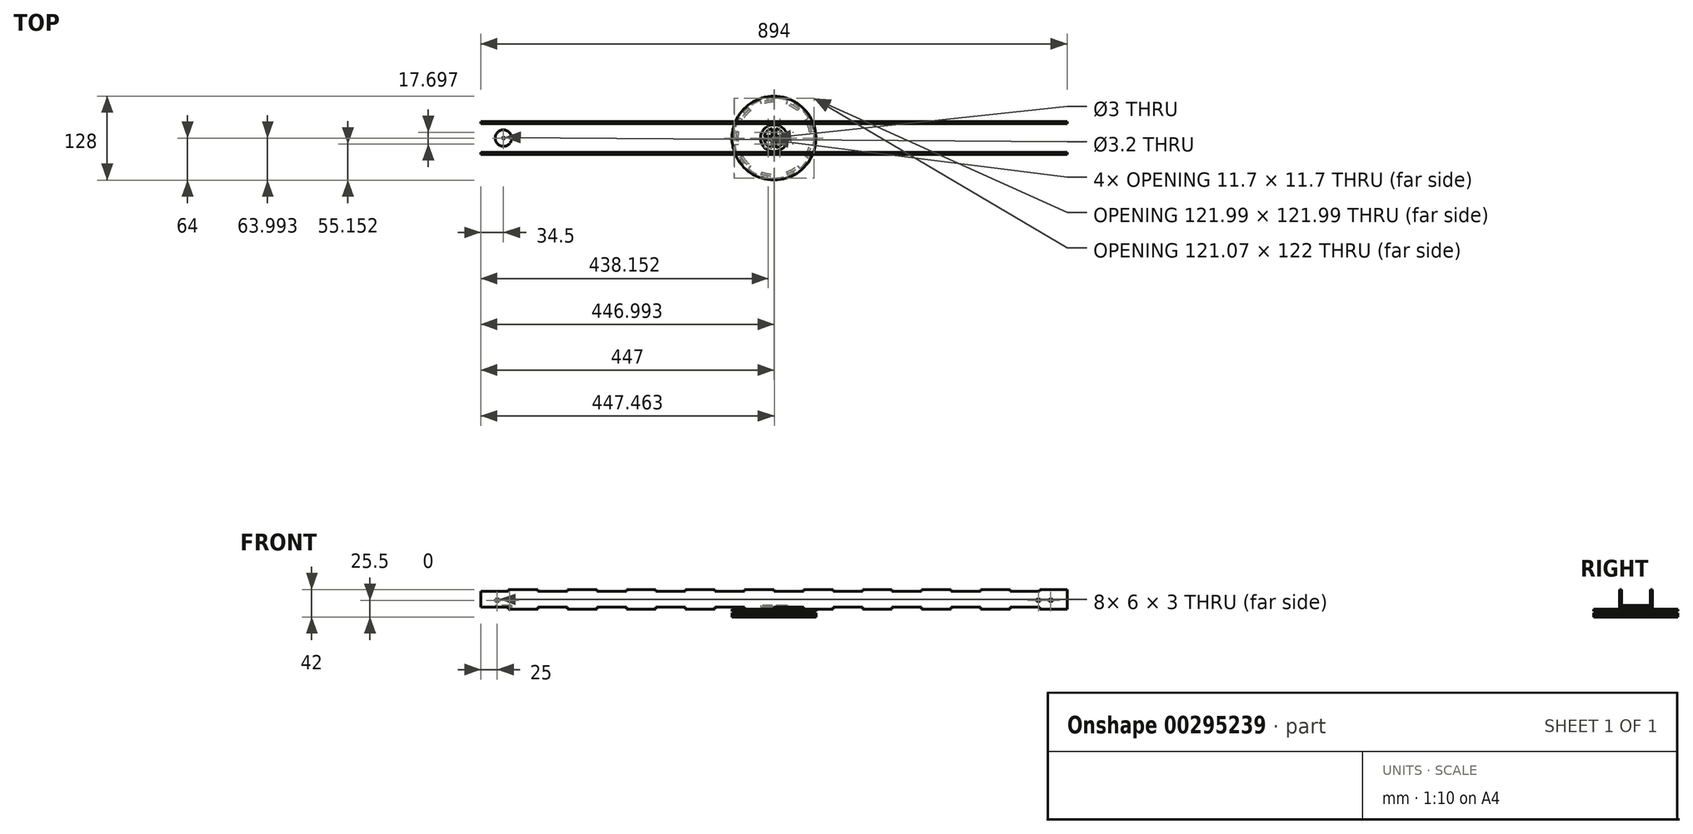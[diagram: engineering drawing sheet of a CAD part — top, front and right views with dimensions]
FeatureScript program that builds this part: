
annotation { "Feature Type Name" : "Feature", "Feature Type Description" : "" }
export const myFeature = defineFeature(function(context is Context, id is Id, definition is map)
    precondition{}
    {
        {
            assignVariable(context, id + "F0", {"name" : "WT", "anyValue" : 3});
        }
        {
            var Q0;
            Q0=qCreatedBy(makeId("Top.planeOp"),FACE);
            var sketch = newSketch(context, id + "F1", { "sketchPlane" : qUnion([Q0])});
            skCircle(sketch, "E0", {"center": v(0, 0) * mm, "radius": 60 * mm});
            skLineSegment(sketch, "E1.bottom", {"start": v(-450, 25) * mm, "end": v(450, 25) * mm});
            skLineSegment(sketch, "E1.top", {"start": v(-450, -25) * mm, "end": v(450, -25) * mm});
            skLineSegment(sketch, "E1.left", {"start": v(-450, 25) * mm, "end": v(-450, -25) * mm});
            skLineSegment(sketch, "E1.right", {"start": v(450, 25) * mm, "end": v(450, -25) * mm});
            skLineSegment(sketch, "E2", {"start": v(-450, 0) * mm, "end": v(450, 0) * mm, "construction": true});
            skCircle(sketch, "E3", {"center": v(-412.5, 0) * mm, "radius": 12.5 * mm});
            skCircle(sketch, "E4", {"center": v(0, 0) * mm, "radius": 64 * mm});
            skCircle(sketch, "E5", {"center": v(0, 0) * mm, "radius": 30 * mm});
            skCircle(sketch, "E6", {"center": v(0, 0) * mm, "radius": 27 * mm});
            skLineSegment(sketch, "E7", {"start": v(-30, 0) * mm, "end": v(0, 0) * mm});
            skLineSegment(sketch, "E8", {"start": v(0, 30) * mm, "end": v(0, 0) * mm});
            skLineSegment(sketch, "E9", {"start": v(0, 0) * mm, "end": v(30, 0) * mm});
            skLineSegment(sketch, "E10", {"start": v(0, 0) * mm, "end": v(0, -30) * mm});
            skPoint(sketch, "E10.endSnap0", {"position": v(0, -25) * mm});
            skLineSegment(sketch, "E11.bottom", {"start": v(-375, 10) * mm, "end": v(375, 10) * mm});
            skLineSegment(sketch, "E11.top", {"start": v(-375, -10) * mm, "end": v(375, -10) * mm});
            skLineSegment(sketch, "E11.left", {"start": v(-375, 10) * mm, "end": v(-375, -10) * mm});
            skLineSegment(sketch, "E11.right", {"start": v(375, 10) * mm, "end": v(375, -10) * mm});
            skLineSegment(sketch, "E12.bottom", {"start": v(-447, 22) * mm, "end": v(447, 22) * mm});
            skLineSegment(sketch, "E12.top", {"start": v(-447, -22) * mm, "end": v(447, -22) * mm});
            skLineSegment(sketch, "E12.left", {"start": v(-447, 22) * mm, "end": v(-447, -22) * mm});
            skLineSegment(sketch, "E12.right", {"start": v(447, 22) * mm, "end": v(447, -22) * mm});
            skCircle(sketch, "E13.MirrorC", {"center": v(412.5, 0) * mm, "radius": 12.5 * mm});
            skSolve(sketch);
        }
        {
            var Q0;
            Q0=qCreatedBy(makeId("Top.planeOp"),FACE);
            cPlane(context, id + "F2", {"entities" : qUnion([Q0]), "cplaneType" : CPlaneType.OFFSET, "offset" : (getVariable(context, 'WT')) * mm, "width" : 150 * mm, "height" : 150 * mm});
        }
        {
            var Q0;
            Q0=qCreatedBy(makeId("Top.planeOp"),FACE);
            var sketch = newSketch(context, id + "F3", { "sketchPlane" : qUnion([Q0])});
            skCircle(sketch, "E14.0", {"center": v(0, 0) * mm, "radius": 64 * mm});
            skLineSegment(sketch, "E15.0", {"start": v(-450, 25) * mm, "end": v(450, 25) * mm, "construction": true});
            skLineSegment(sketch, "E16.0", {"start": v(-450, -25) * mm, "end": v(450, -25) * mm, "construction": true});
            skCircle(sketch, "E17", {"center": v(0, 0) * mm, "radius": 15 * mm});
            skLineSegment(sketch, "E18.0", {"start": v(-447, 22) * mm, "end": v(447, 22) * mm, "construction": true});
            skLineSegment(sketch, "E18.1", {"start": v(-447, -22) * mm, "end": v(447, -22) * mm, "construction": true});
            skLineSegment(sketch, "E19.0", {"start": v(-375, -10) * mm, "end": v(375, -10) * mm, "construction": true});
            skLineSegment(sketch, "E19.1", {"start": v(-375, 10) * mm, "end": v(375, 10) * mm, "construction": true});
            skLineSegment(sketch, "E20", {"start": v(-15, 0) * mm, "end": v(15, 0) * mm, "construction": true});
            skLineSegment(sketch, "E21", {"start": v(-14.7, 3) * mm, "end": v(14.7, 3) * mm});
            skLineSegment(sketch, "E22.MirrorCS", {"start": v(-14.7, -3) * mm, "end": v(14.7, -3) * mm});
            skLineSegment(sketch, "E23", {"start": v(-3, 3) * mm, "end": v(-3, 14.7) * mm});
            skLineSegment(sketch, "E24.MirrorCS", {"start": v(3, 3) * mm, "end": v(3, 14.7) * mm});
            skLineSegment(sketch, "E25.MirrorCS", {"start": v(-3, -3) * mm, "end": v(-3, -14.7) * mm});
            skLineSegment(sketch, "E26.MirrorCS", {"start": v(3, -3) * mm, "end": v(3, -14.7) * mm});
            skCircle(sketch, "E27", {"center": v(0, 0) * mm, "radius": 20.5 * mm});
            skCircle(sketch, "E28", {"center": v(0, 0) * mm, "radius": 1.5 * mm});
            skLineSegment(sketch, "E29", {"start": v(-3, 3) * mm, "end": v(-3, -3) * mm});
            skLineSegment(sketch, "E30", {"start": v(3, -3) * mm, "end": v(3, 3) * mm});
            skLineSegment(sketch, "E31", {"start": v(-3, -9.5) * mm, "end": v(3, -9.5) * mm});
            skLineSegment(sketch, "E32.MirrorCS", {"start": v(-3, 9.5) * mm, "end": v(3, 9.5) * mm});
            skSolve(sketch);
        }
        {
            var Q0;
            Q0=qCreatedBy(makeId("Top.planeOp"),FACE);
            cPlane(context, id + "F4", {"entities" : qUnion([Q0]), "cplaneType" : CPlaneType.OFFSET, "offset" : (getVariable(context, 'WT')) * mm, "width" : 150 * mm, "height" : 150 * mm});
        }
        {
            var Q0;
            Q0=qCreatedBy(id+"F4.planeOp",FACE);
            var sketch = newSketch(context, id + "F5", { "sketchPlane" : qUnion([Q0])});
            skCircle(sketch, "E33.0", {"center": v(0, 0) * mm, "radius": 20.5 * mm});
            skCircle(sketch, "E34.0", {"center": v(0, 0) * mm, "radius": 15 * mm});
            skLineSegment(sketch, "E35.0", {"start": v(3, -3) * mm, "end": v(3, -14.7) * mm});
            skLineSegment(sketch, "E35.1", {"start": v(-3, -3) * mm, "end": v(-3, -14.7) * mm});
            skLineSegment(sketch, "E35.2", {"start": v(-14.7, -3) * mm, "end": v(14.7, -3) * mm});
            skLineSegment(sketch, "E35.3", {"start": v(-14.7, 3) * mm, "end": v(14.7, 3) * mm});
            skLineSegment(sketch, "E35.4", {"start": v(-3, 3) * mm, "end": v(-3, 14.7) * mm});
            skLineSegment(sketch, "E35.5", {"start": v(3, 3) * mm, "end": v(3, 14.7) * mm});
            skSolve(sketch);
        }
        {
            var Q0;
            Q0=qCreatedBy(id+"F2.planeOp",FACE);
            var sketch = newSketch(context, id + "F6", { "sketchPlane" : qUnion([Q0])});
            skLineSegment(sketch, "E36.0", {"start": v(-450, 25) * mm, "end": v(450, 25) * mm});
            skLineSegment(sketch, "E36.1", {"start": v(-447, 22) * mm, "end": v(447, 22) * mm});
            skLineSegment(sketch, "E36.2", {"start": v(-375, 10) * mm, "end": v(375, 10) * mm});
            skLineSegment(sketch, "E36.3", {"start": v(-375, -10) * mm, "end": v(375, -10) * mm});
            skLineSegment(sketch, "E36.4", {"start": v(-447, -22) * mm, "end": v(447, -22) * mm});
            skLineSegment(sketch, "E36.5", {"start": v(-450, -25) * mm, "end": v(450, -25) * mm});
            skLineSegment(sketch, "E36.6", {"start": v(375, 10) * mm, "end": v(375, -10) * mm});
            skLineSegment(sketch, "E36.7", {"start": v(447, 22) * mm, "end": v(447, -22) * mm});
            skLineSegment(sketch, "E36.8", {"start": v(450, 25) * mm, "end": v(450, -25) * mm});
            skLineSegment(sketch, "E36.9", {"start": v(-375, 10) * mm, "end": v(-375, -10) * mm});
            skLineSegment(sketch, "E36.10", {"start": v(-447, 22) * mm, "end": v(-447, -22) * mm});
            skLineSegment(sketch, "E36.11", {"start": v(-450, 25) * mm, "end": v(-450, -25) * mm});
            skCircle(sketch, "E37.0", {"center": v(-412.5, 0) * mm, "radius": 12.5 * mm});
            skCircle(sketch, "E38", {"center": v(-412.5, 0) * mm, "radius": 1.6 * mm});
            skLineSegment(sketch, "E39", {"start": v(-450, 8.33) * mm, "end": v(-447, 8.33) * mm});
            skLineSegment(sketch, "E40", {"start": v(-450, -8.33) * mm, "end": v(-447, -8.33) * mm});
            skPoint(sketch, "E40.endSnap0", {"position": v(-447, 0) * mm});
            skLineSegment(sketch, "E41", {"start": v(0, 22) * mm, "end": v(0, 25) * mm});
            skLineSegment(sketch, "E42", {"start": v(-447, 22) * mm, "end": v(-450, 22) * mm});
            skLineSegment(sketch, "E43", {"start": v(-447, -22) * mm, "end": v(-450, -22) * mm});
            skLineSegment(sketch, "E44", {"start": v(-405, 22) * mm, "end": v(-405, 25) * mm});
            skLineSegment(sketch, "E45.0.1.0", {"start": v(-405, -25) * mm, "end": v(-405, -22) * mm});
            skLineSegment(sketch, "E45.1.0.0", {"start": v(-360, 22) * mm, "end": v(-360, 25) * mm});
            skLineSegment(sketch, "E45.1.1.0", {"start": v(-360, -25) * mm, "end": v(-360, -22) * mm});
            skLineSegment(sketch, "E45.2.0.0", {"start": v(-315, 22) * mm, "end": v(-315, 25) * mm});
            skLineSegment(sketch, "E45.2.1.0", {"start": v(-315, -25) * mm, "end": v(-315, -22) * mm});
            skLineSegment(sketch, "E45.3.0.0", {"start": v(-270, 22) * mm, "end": v(-270, 25) * mm});
            skLineSegment(sketch, "E45.3.1.0", {"start": v(-270, -25) * mm, "end": v(-270, -22) * mm});
            skLineSegment(sketch, "E45.4.0.0", {"start": v(-225, 22) * mm, "end": v(-225, 25) * mm});
            skLineSegment(sketch, "E45.4.1.0", {"start": v(-225, -25) * mm, "end": v(-225, -22) * mm});
            skLineSegment(sketch, "E45.5.0.0", {"start": v(-180, 22) * mm, "end": v(-180, 25) * mm});
            skLineSegment(sketch, "E45.5.1.0", {"start": v(-180, -25) * mm, "end": v(-180, -22) * mm});
            skLineSegment(sketch, "E45.6.0.0", {"start": v(-135, 22) * mm, "end": v(-135, 25) * mm});
            skLineSegment(sketch, "E45.6.1.0", {"start": v(-135, -25) * mm, "end": v(-135, -22) * mm});
            skLineSegment(sketch, "E45.7.0.0", {"start": v(-90, 22) * mm, "end": v(-90, 25) * mm});
            skLineSegment(sketch, "E45.7.1.0", {"start": v(-90, -25) * mm, "end": v(-90, -22) * mm});
            skLineSegment(sketch, "E45.8.0.0", {"start": v(-45, 22) * mm, "end": v(-45, 25) * mm});
            skLineSegment(sketch, "E45.8.1.0", {"start": v(-45, -25) * mm, "end": v(-45, -22) * mm});
            skLineSegment(sketch, "E45.9.1.0", {"start": v(0, -25) * mm, "end": v(0, -22) * mm});
            skLineSegment(sketch, "E45.10.0.0", {"start": v(45, 22) * mm, "end": v(45, 25) * mm});
            skLineSegment(sketch, "E45.10.1.0", {"start": v(45, -25) * mm, "end": v(45, -22) * mm});
            skLineSegment(sketch, "E45.11.0.0", {"start": v(90, 22) * mm, "end": v(90, 25) * mm});
            skLineSegment(sketch, "E45.11.1.0", {"start": v(90, -25) * mm, "end": v(90, -22) * mm});
            skLineSegment(sketch, "E45.12.0.0", {"start": v(135, 22) * mm, "end": v(135, 25) * mm});
            skLineSegment(sketch, "E45.12.1.0", {"start": v(135, -25) * mm, "end": v(135, -22) * mm});
            skLineSegment(sketch, "E45.13.0.0", {"start": v(180, 22) * mm, "end": v(180, 25) * mm});
            skLineSegment(sketch, "E45.13.1.0", {"start": v(180, -25) * mm, "end": v(180, -22) * mm});
            skLineSegment(sketch, "E45.14.0.0", {"start": v(225, 22) * mm, "end": v(225, 25) * mm});
            skLineSegment(sketch, "E45.14.1.0", {"start": v(225, -25) * mm, "end": v(225, -22) * mm});
            skLineSegment(sketch, "E45.15.0.0", {"start": v(270, 22) * mm, "end": v(270, 25) * mm});
            skLineSegment(sketch, "E45.15.1.0", {"start": v(270, -25) * mm, "end": v(270, -22) * mm});
            skLineSegment(sketch, "E45.16.0.0", {"start": v(315, 22) * mm, "end": v(315, 25) * mm});
            skLineSegment(sketch, "E45.16.1.0", {"start": v(315, -25) * mm, "end": v(315, -22) * mm});
            skLineSegment(sketch, "E45.17.0.0", {"start": v(360, 22) * mm, "end": v(360, 25) * mm});
            skLineSegment(sketch, "E45.17.1.0", {"start": v(360, -25) * mm, "end": v(360, -22) * mm});
            skLineSegment(sketch, "E45.18.0.0", {"start": v(405, 22) * mm, "end": v(405, 25) * mm});
            skLineSegment(sketch, "E45.18.1.0", {"start": v(405, -25) * mm, "end": v(405, -22) * mm});
            skLineSegment(sketch, "E45.direction1", {"start": v(-405, 22) * mm, "end": v(-360, 22) * mm, "construction": true});
            skLineSegment(sketch, "E45.direction2", {"start": v(-405, 22) * mm, "end": v(-405, -25) * mm, "construction": true});
            skLineSegment(sketch, "E46.MirrorCS", {"start": v(447, 22) * mm, "end": v(450, 22) * mm});
            skLineSegment(sketch, "E47.MirrorCS", {"start": v(450, 8.33) * mm, "end": v(447, 8.33) * mm});
            skLineSegment(sketch, "E48.MirrorCS", {"start": v(450, -8.33) * mm, "end": v(447, -8.33) * mm});
            skLineSegment(sketch, "E49.MirrorCS", {"start": v(447, -22) * mm, "end": v(450, -22) * mm});
            skCircle(sketch, "E50", {"center": v(-435.5, 0) * mm, "radius": 2.5 * mm});
            skCircle(sketch, "E51", {"center": v(-386.6, -10.4) * mm, "radius": 1.6 * mm});
            skLineSegment(sketch, "E52", {"start": v(-400, 0) * mm, "end": v(-375, 0) * mm, "construction": true});
            skPoint(sketch, "E52.startSnap0", {"position": v(-450, 0) * mm});
            skCircle(sketch, "E53.MirrorC", {"center": v(-386.6, 10.4) * mm, "radius": 1.6 * mm});
            skCircle(sketch, "E54.MirrorC", {"center": v(386.6, 10.4) * mm, "radius": 1.6 * mm});
            skCircle(sketch, "E55.MirrorC", {"center": v(386.6, -10.4) * mm, "radius": 1.6 * mm});
            skCircle(sketch, "E56.MirrorC", {"center": v(412.5, 0) * mm, "radius": 1.6 * mm});
            skCircle(sketch, "E57.MirrorC", {"center": v(412.5, 0) * mm, "radius": 12.5 * mm});
            skCircle(sketch, "E58.MirrorC", {"center": v(435.5, 0) * mm, "radius": 2.5 * mm});
            skSolve(sketch);
        }
        {
            var Q0;
            Q0=sQuery(id+"F1.wireOp",EDGE,"E1.top");
            cPlane(context, id + "F7", {"entities" : qUnion([Q0]), "cplaneType" : CPlaneType.LINE_ANGLE, "offset" : 25 * mm, "angle" : 0 * degree, "width" : 150 * mm, "height" : 150 * mm});
        }
        {
            var Q0;
            Q0=qCreatedBy(id+"F7.planeOp",FACE);
            var sketch = newSketch(context, id + "F8", { "sketchPlane" : qUnion([Q0])});
            skLineSegment(sketch, "E59.0", {"start": v(450, 0) * mm, "end": v(-450, 0) * mm});
            skLineSegment(sketch, "E60", {"start": v(450, 0) * mm, "end": v(450, 30) * mm});
            skLineSegment(sketch, "E61", {"start": v(450, 30) * mm, "end": v(-450, 30) * mm});
            skLineSegment(sketch, "E62", {"start": v(-450, 30) * mm, "end": v(-450, 0) * mm});
            skSolve(sketch);
        }
        {
            var Q0;
            Q0=sQuery(id+"F1.wireOp",EDGE,"E1.bottom");
            cPlane(context, id + "F9", {"entities" : qUnion([Q0]), "cplaneType" : CPlaneType.LINE_ANGLE, "offset" : 25 * mm, "angle" : 0 * degree, "width" : 150 * mm, "height" : 150 * mm});
        }
        {
            var Q0;
            Q0=qCreatedBy(id+"F9.planeOp",FACE);
            var sketch = newSketch(context, id + "F10", { "sketchPlane" : qUnion([Q0])});
            skLineSegment(sketch, "E63.0", {"start": v(450, 0) * mm, "end": v(-450, 0) * mm});
            skLineSegment(sketch, "E64.0", {"start": v(-450, 30) * mm, "end": v(-450, 0) * mm});
            skLineSegment(sketch, "E64.1", {"start": v(450, 30) * mm, "end": v(-450, 30) * mm});
            skLineSegment(sketch, "E64.2", {"start": v(450, 0) * mm, "end": v(450, 30) * mm});
            skSolve(sketch);
        }
        {
            var Q0;
            Q0=sQuery(id+"F1.wireOp",EDGE,"E1.right");
            cPlane(context, id + "F11", {"entities" : qUnion([Q0]), "cplaneType" : CPlaneType.LINE_ANGLE, "offset" : 25 * mm, "angle" : 90 * degree, "width" : 150 * mm, "height" : 150 * mm});
        }
        {
            var Q0;
            Q0=qCreatedBy(id+"F11.planeOp",FACE);
            var sketch = newSketch(context, id + "F12", { "sketchPlane" : qUnion([Q0])});
            skLineSegment(sketch, "E65.0", {"start": v(25, 0) * mm, "end": v(-25, 0) * mm});
            skLineSegment(sketch, "E66.0", {"start": v(-25, 30) * mm, "end": v(-25, 0) * mm});
            skLineSegment(sketch, "E67", {"start": v(-25, 30) * mm, "end": v(25, 30) * mm});
            skLineSegment(sketch, "E68", {"start": v(25, 30) * mm, "end": v(25, 0) * mm});
            skSolve(sketch);
        }
        {
            var Q0;
            Q0=sQuery(id+"F1.wireOp",EDGE,"E1.left");
            cPlane(context, id + "F13", {"entities" : qUnion([Q0]), "cplaneType" : CPlaneType.LINE_ANGLE, "offset" : 25 * mm, "angle" : 90 * degree, "width" : 150 * mm, "height" : 150 * mm});
        }
        {
            var Q0;
            Q0=qCreatedBy(id+"F13.planeOp",FACE);
            var sketch = newSketch(context, id + "F14", { "sketchPlane" : qUnion([Q0])});
            skLineSegment(sketch, "E69.0", {"start": v(25, 0) * mm, "end": v(-25, 0) * mm});
            skLineSegment(sketch, "E70.0", {"start": v(25, 30) * mm, "end": v(25, 0) * mm});
            skLineSegment(sketch, "E71.0", {"start": v(-25, 30) * mm, "end": v(25, 30) * mm});
            skLineSegment(sketch, "E72.0", {"start": v(-25, 30) * mm, "end": v(-25, 0) * mm});
            skSolve(sketch);
        }
        {
            var Q0;
            Q0=sQuery(id+"F8.wireOp",EDGE,"E61");
            cPlane(context, id + "F15", {"entities" : qUnion([Q0]), "cplaneType" : CPlaneType.LINE_ANGLE, "offset" : 25 * mm, "angle" : 90 * degree, "width" : 150 * mm, "height" : 150 * mm});
        }
        {
            var Q0;
            Q0=qCreatedBy(id+"F15.planeOp",FACE);
            var sketch = newSketch(context, id + "F16", { "sketchPlane" : qUnion([Q0])});
            skLineSegment(sketch, "E73.0", {"start": v(-450, 25) * mm, "end": v(450, 25) * mm});
            skLineSegment(sketch, "E73.1", {"start": v(-450, -25) * mm, "end": v(450, -25) * mm});
            skLineSegment(sketch, "E73.2", {"start": v(450, 25) * mm, "end": v(450, -25) * mm});
            skLineSegment(sketch, "E73.3", {"start": v(-450, 25) * mm, "end": v(-450, -25) * mm});
            skLineSegment(sketch, "E74.0", {"start": v(-447, 22) * mm, "end": v(-447, -22) * mm});
            skLineSegment(sketch, "E75.0", {"start": v(-447, 22) * mm, "end": v(-450, 22) * mm});
            skLineSegment(sketch, "E75.1", {"start": v(-450, 8.33) * mm, "end": v(-447, 8.33) * mm});
            skLineSegment(sketch, "E75.2", {"start": v(-450, -8.33) * mm, "end": v(-447, -8.33) * mm});
            skLineSegment(sketch, "E75.3", {"start": v(-447, -22) * mm, "end": v(-450, -22) * mm});
            skLineSegment(sketch, "E76.0", {"start": v(-447, -22) * mm, "end": v(447, -22) * mm});
            skLineSegment(sketch, "E77.0", {"start": v(-447, 22) * mm, "end": v(447, 22) * mm});
            skLineSegment(sketch, "E78.0", {"start": v(-405, 22) * mm, "end": v(-405, 25) * mm});
            skLineSegment(sketch, "E78.1", {"start": v(-405, -25) * mm, "end": v(-405, -22) * mm});
            skLineSegment(sketch, "E78.2", {"start": v(-360, 22) * mm, "end": v(-360, 25) * mm});
            skLineSegment(sketch, "E78.3", {"start": v(-360, -25) * mm, "end": v(-360, -22) * mm});
            skLineSegment(sketch, "E78.4", {"start": v(-315, -25) * mm, "end": v(-315, -22) * mm});
            skLineSegment(sketch, "E78.5", {"start": v(-315, 22) * mm, "end": v(-315, 25) * mm});
            skLineSegment(sketch, "E78.6", {"start": v(-270, 22) * mm, "end": v(-270, 25) * mm});
            skLineSegment(sketch, "E78.7", {"start": v(-270, -25) * mm, "end": v(-270, -22) * mm});
            skLineSegment(sketch, "E78.8", {"start": v(-225, -25) * mm, "end": v(-225, -22) * mm});
            skLineSegment(sketch, "E78.9", {"start": v(-225, 22) * mm, "end": v(-225, 25) * mm});
            skLineSegment(sketch, "E78.10", {"start": v(-180, 22) * mm, "end": v(-180, 25) * mm});
            skLineSegment(sketch, "E78.11", {"start": v(-180, -25) * mm, "end": v(-180, -22) * mm});
            skLineSegment(sketch, "E78.12", {"start": v(-135, 22) * mm, "end": v(-135, 25) * mm});
            skLineSegment(sketch, "E78.13", {"start": v(-135, -25) * mm, "end": v(-135, -22) * mm});
            skLineSegment(sketch, "E78.14", {"start": v(-90, 22) * mm, "end": v(-90, 25) * mm});
            skLineSegment(sketch, "E78.15", {"start": v(-90, -25) * mm, "end": v(-90, -22) * mm});
            skLineSegment(sketch, "E78.16", {"start": v(-45, 22) * mm, "end": v(-45, 25) * mm});
            skLineSegment(sketch, "E78.17", {"start": v(-45, -25) * mm, "end": v(-45, -22) * mm});
            skLineSegment(sketch, "E78.18", {"start": v(0, 22) * mm, "end": v(0, 25) * mm});
            skLineSegment(sketch, "E78.19", {"start": v(0, -25) * mm, "end": v(0, -22) * mm});
            skLineSegment(sketch, "E78.20", {"start": v(45, 22) * mm, "end": v(45, 25) * mm});
            skLineSegment(sketch, "E78.21", {"start": v(45, -25) * mm, "end": v(45, -22) * mm});
            skLineSegment(sketch, "E79.0", {"start": v(90, 22) * mm, "end": v(90, 25) * mm});
            skLineSegment(sketch, "E79.1", {"start": v(90, -25) * mm, "end": v(90, -22) * mm});
            skLineSegment(sketch, "E79.2", {"start": v(135, 22) * mm, "end": v(135, 25) * mm});
            skLineSegment(sketch, "E79.3", {"start": v(135, -25) * mm, "end": v(135, -22) * mm});
            skLineSegment(sketch, "E79.4", {"start": v(180, 22) * mm, "end": v(180, 25) * mm});
            skLineSegment(sketch, "E79.5", {"start": v(180, -25) * mm, "end": v(180, -22) * mm});
            skLineSegment(sketch, "E79.6", {"start": v(225, 22) * mm, "end": v(225, 25) * mm});
            skLineSegment(sketch, "E79.7", {"start": v(225, -25) * mm, "end": v(225, -22) * mm});
            skPoint(sketch, "E79.8", {"position": v(225, -23.5) * mm});
            skLineSegment(sketch, "E80.0", {"start": v(270, 22) * mm, "end": v(270, 25) * mm});
            skLineSegment(sketch, "E80.1", {"start": v(270, -25) * mm, "end": v(270, -22) * mm});
            skLineSegment(sketch, "E80.2", {"start": v(315, 22) * mm, "end": v(315, 25) * mm});
            skLineSegment(sketch, "E80.3", {"start": v(315, -25) * mm, "end": v(315, -22) * mm});
            skLineSegment(sketch, "E80.4", {"start": v(360, 22) * mm, "end": v(360, 25) * mm});
            skLineSegment(sketch, "E80.5", {"start": v(360, -25) * mm, "end": v(360, -22) * mm});
            skLineSegment(sketch, "E80.6", {"start": v(405, 22) * mm, "end": v(405, 25) * mm});
            skLineSegment(sketch, "E80.7", {"start": v(405, -25) * mm, "end": v(405, -22) * mm});
            skLineSegment(sketch, "E80.8", {"start": v(450, 8.33) * mm, "end": v(447, 8.33) * mm});
            skLineSegment(sketch, "E80.9", {"start": v(447, 22) * mm, "end": v(450, 22) * mm});
            skLineSegment(sketch, "E80.10", {"start": v(450, -8.33) * mm, "end": v(447, -8.33) * mm});
            skLineSegment(sketch, "E80.11", {"start": v(447, -22) * mm, "end": v(450, -22) * mm});
            skLineSegment(sketch, "E81.0", {"start": v(447, 22) * mm, "end": v(447, -22) * mm});
            skSolve(sketch);
        }
        {
            var Q0;
            Q0=qCreatedBy(id+"F2.planeOp",FACE);
            cPlane(context, id + "F17", {"entities" : qUnion([Q0]), "cplaneType" : CPlaneType.OFFSET, "offset" : (getVariable(context, 'WT')) * 3 * mm, "width" : 150 * mm, "height" : 150 * mm});
        }
        {
            var Q0;
            Q0=qCreatedBy(id+"F17.planeOp",FACE);
            var sketch = newSketch(context, id + "F18", { "sketchPlane" : qUnion([Q0])});
            skCircle(sketch, "E82.0", {"center": v(-412.5, 0) * mm, "radius": 1.6 * mm});
            skCircle(sketch, "E83.0", {"center": v(-412.5, 0) * mm, "radius": 12.5 * mm, "construction": true});
            skLineSegment(sketch, "E84.0", {"start": v(-450, 25) * mm, "end": v(450, 25) * mm});
            skLineSegment(sketch, "E85.0", {"start": v(-450, -25) * mm, "end": v(450, -25) * mm});
            skLineSegment(sketch, "E86", {"start": v(-425, -25) * mm, "end": v(-425, 25) * mm});
            skLineSegment(sketch, "E87", {"start": v(-400, 25) * mm, "end": v(-400, -25) * mm});
            skLineSegment(sketch, "E88.0", {"start": v(-447, -22) * mm, "end": v(-425, -22) * mm, "construction": true});
            skLineSegment(sketch, "E89", {"start": v(-419, 25) * mm, "end": v(-419, 22) * mm});
            skLineSegment(sketch, "E90", {"start": v(-412.5, 0) * mm, "end": v(-412.5, 12.5) * mm, "construction": true});
            skLineSegment(sketch, "E91.MirrorCS", {"start": v(-406, 25) * mm, "end": v(-406, 22) * mm});
            skLineSegment(sketch, "E92.MirrorCS", {"start": v(-406, -25) * mm, "end": v(-406, -22) * mm});
            skLineSegment(sketch, "E93.MirrorCS", {"start": v(-419, -25) * mm, "end": v(-419, -22) * mm});
            skLineSegment(sketch, "E94.0", {"start": v(-447, 22) * mm, "end": v(-425, 22) * mm});
            skPoint(sketch, "E95.start.orphan", {"position": v(-425, 22) * mm});
            skPoint(sketch, "E96.MirrorCS.end.orphan", {"position": v(-406, 22) * mm});
            skPoint(sketch, "E96.MirrorCS.start.orphan", {"position": v(-400, 22) * mm});
            skLineSegment(sketch, "E97.trimOffspring", {"start": v(-400, 22) * mm, "end": v(400, 22) * mm});
            skLineSegment(sketch, "E98.trimOffspring", {"start": v(-419, 22) * mm, "end": v(-406, 22) * mm});
            skLineSegment(sketch, "E99.trimOffspring", {"start": v(-419, -22) * mm, "end": v(-406, -22) * mm});
            skPoint(sketch, "E100.MirrorCS.end.orphan", {"position": v(-419, -22) * mm});
            skLineSegment(sketch, "E101.trimOffspring", {"start": v(-400, -22) * mm, "end": v(447, -22) * mm, "construction": true});
            skLineSegment(sketch, "E102.MirrorCS", {"start": v(425, -25) * mm, "end": v(425, 25) * mm});
            skLineSegment(sketch, "E103.MirrorCS", {"start": v(419, 25) * mm, "end": v(419, 22) * mm});
            skLineSegment(sketch, "E104.MirrorCS", {"start": v(419, 22) * mm, "end": v(406, 22) * mm});
            skLineSegment(sketch, "E105.MirrorCS", {"start": v(406, 25) * mm, "end": v(406, 22) * mm});
            skLineSegment(sketch, "E106.MirrorCS", {"start": v(400, 25) * mm, "end": v(400, -25) * mm});
            skLineSegment(sketch, "E107.MirrorCS", {"start": v(406, -25) * mm, "end": v(406, -22) * mm});
            skLineSegment(sketch, "E108.MirrorCS", {"start": v(419, -22) * mm, "end": v(406, -22) * mm});
            skLineSegment(sketch, "E109.MirrorCS", {"start": v(419, -25) * mm, "end": v(419, -22) * mm});
            skCircle(sketch, "E110.0", {"center": v(412.5, 0) * mm, "radius": 1.6 * mm});
            skLineSegment(sketch, "E111.trimOffspring", {"start": v(406, 22) * mm, "end": v(419, 22) * mm});
            skLineSegment(sketch, "E112.trimOffspring", {"start": v(425, 22) * mm, "end": v(447, 22) * mm});
            skSolve(sketch);
        }
        {
            var Q0;
            Q0=qCreatedBy(makeId("Top.planeOp"),FACE);
            cPlane(context, id + "F19", {"entities" : qUnion([Q0]), "cplaneType" : CPlaneType.OFFSET, "offset" : (getVariable(context, 'WT') * 2) * mm, "oppositeDirection" : true, "width" : 150 * mm, "height" : 150 * mm});
        }
        {
            var Q0;
            Q0=qCreatedBy(makeId("Top.planeOp"),FACE);
            cPlane(context, id + "F20", {"entities" : qUnion([Q0]), "cplaneType" : CPlaneType.OFFSET, "offset" : (getVariable(context, 'WT') * 3) * mm, "oppositeDirection" : true, "width" : 150 * mm, "height" : 150 * mm});
        }
        {
            var Q0;
            Q0=qCreatedBy(id+"F20.planeOp",FACE);
            var sketch = newSketch(context, id + "F21", { "sketchPlane" : qUnion([Q0])});
            skCircle(sketch, "E113.0", {"center": v(0, 0) * mm, "radius": 64 * mm});
            skCircle(sketch, "E114", {"center": v(0, 0) * mm, "radius": 61 * mm});
            skCircle(sketch, "E115", {"center": v(0, 0) * mm, "radius": 58 * mm});
            skCircle(sketch, "E116", {"center": v(0, 0) * mm, "radius": 55 * mm});
            skLineSegment(sketch, "E117", {"start": v(0, -64) * mm, "end": v(0, -61) * mm, "construction": true});
            skLineSegment(sketch, "E118", {"start": v(0, -61) * mm, "end": v(0, -58) * mm, "construction": true});
            skLineSegment(sketch, "E119", {"start": v(0, -58) * mm, "end": v(0, -55) * mm, "construction": true});
            skLineSegment(sketch, "E120", {"start": v(0, 0) * mm, "end": v(10.6, -60.07) * mm});
            skLineSegment(sketch, "E121", {"start": v(0, 0) * mm, "end": v(0, -61) * mm});
            skLineSegment(sketch, "E122.1.0", {"start": v(0, 0) * mm, "end": v(20.86, -57.32) * mm});
            skLineSegment(sketch, "E122.2.0", {"start": v(0, 0) * mm, "end": v(30.5, -52.83) * mm});
            skLineSegment(sketch, "E122.3.0", {"start": v(0, 0) * mm, "end": v(39.21, -46.73) * mm});
            skLineSegment(sketch, "E122.4.0", {"start": v(0, 0) * mm, "end": v(46.73, -39.21) * mm});
            skLineSegment(sketch, "E122.5.0", {"start": v(0, 0) * mm, "end": v(52.83, -30.5) * mm});
            skLineSegment(sketch, "E122.6.0", {"start": v(0, 0) * mm, "end": v(57.32, -20.86) * mm});
            skLineSegment(sketch, "E122.7.0", {"start": v(0, 0) * mm, "end": v(60.07, -10.6) * mm});
            skLineSegment(sketch, "E122.8.0", {"start": v(0, 0) * mm, "end": v(61, 0) * mm});
            skLineSegment(sketch, "E122.9.0", {"start": v(0, 0) * mm, "end": v(60.07, 10.6) * mm});
            skLineSegment(sketch, "E122.10.0", {"start": v(0, 0) * mm, "end": v(57.32, 20.86) * mm});
            skLineSegment(sketch, "E122.11.0", {"start": v(0, 0) * mm, "end": v(52.83, 30.5) * mm});
            skLineSegment(sketch, "E122.12.0", {"start": v(0, 0) * mm, "end": v(46.73, 39.21) * mm});
            skLineSegment(sketch, "E122.13.0", {"start": v(0, 0) * mm, "end": v(39.21, 46.73) * mm});
            skLineSegment(sketch, "E122.14.0", {"start": v(0, 0) * mm, "end": v(30.5, 52.83) * mm});
            skLineSegment(sketch, "E122.15.0", {"start": v(0, 0) * mm, "end": v(20.86, 57.32) * mm});
            skLineSegment(sketch, "E122.16.0", {"start": v(0, 0) * mm, "end": v(10.6, 60.07) * mm});
            skLineSegment(sketch, "E122.17.0", {"start": v(0, 0) * mm, "end": v(0, 61) * mm});
            skLineSegment(sketch, "E122.18.0", {"start": v(0, 0) * mm, "end": v(-10.6, 60.07) * mm});
            skLineSegment(sketch, "E122.19.0", {"start": v(0, 0) * mm, "end": v(-20.86, 57.32) * mm});
            skLineSegment(sketch, "E122.20.0", {"start": v(0, 0) * mm, "end": v(-30.5, 52.83) * mm});
            skLineSegment(sketch, "E122.21.0", {"start": v(0, 0) * mm, "end": v(-39.21, 46.73) * mm});
            skLineSegment(sketch, "E122.22.0", {"start": v(0, 0) * mm, "end": v(-46.73, 39.21) * mm});
            skLineSegment(sketch, "E122.23.0", {"start": v(0, 0) * mm, "end": v(-52.83, 30.5) * mm});
            skLineSegment(sketch, "E122.24.0", {"start": v(0, 0) * mm, "end": v(-57.32, 20.86) * mm});
            skLineSegment(sketch, "E122.25.0", {"start": v(0, 0) * mm, "end": v(-60.07, 10.6) * mm});
            skLineSegment(sketch, "E122.26.0", {"start": v(0, 0) * mm, "end": v(-61, 0) * mm});
            skLineSegment(sketch, "E122.27.0", {"start": v(0, 0) * mm, "end": v(-60.07, -10.6) * mm});
            skLineSegment(sketch, "E122.28.0", {"start": v(0, 0) * mm, "end": v(-57.32, -20.86) * mm});
            skLineSegment(sketch, "E122.29.0", {"start": v(0, 0) * mm, "end": v(-52.83, -30.5) * mm});
            skLineSegment(sketch, "E122.30.0", {"start": v(0, 0) * mm, "end": v(-46.73, -39.21) * mm});
            skLineSegment(sketch, "E122.31.0", {"start": v(0, 0) * mm, "end": v(-39.21, -46.73) * mm});
            skLineSegment(sketch, "E122.32.0", {"start": v(0, 0) * mm, "end": v(-30.5, -52.83) * mm});
            skLineSegment(sketch, "E122.33.0", {"start": v(0, 0) * mm, "end": v(-20.86, -57.32) * mm});
            skLineSegment(sketch, "E122.34.0", {"start": v(0, 0) * mm, "end": v(-10.6, -60.07) * mm});
            skCircle(sketch, "E123.0", {"center": v(0, 0) * mm, "radius": 20.5 * mm});
            skCircle(sketch, "E124.0", {"center": v(0, 0) * mm, "radius": 15 * mm});
            skSolve(sketch);
        }
        {
            var Q0;
            Q0=qCreatedBy(id+"F19.planeOp",FACE);
            var sketch = newSketch(context, id + "F22", { "sketchPlane" : qUnion([Q0])});
            skCircle(sketch, "E125.0", {"center": v(0, 0) * mm, "radius": 64 * mm});
            skCircle(sketch, "E126.0", {"center": v(0, 0) * mm, "radius": 20.5 * mm});
            skSolve(sketch);
        }
        {
            var Q0;
            Q0=makeQuery(id+"F3.imprint","IMPRINT",FACE,{"disambiguationData":[TD([[makeQuery(id+"F3.imprint","IMPRINT",EDGE,{"derivedFrom":sQuery(id+"F3.wireOp",EDGE,"E14.0")}),1.0]])]});
            var Q1;
            Q1=makeQuery(id+"F3.imprint","IMPRINT",FACE,{"disambiguationData":[TD([[makeQuery(id+"F3.imprint","IMPRINT",EDGE,{"derivedFrom":sQuery(id+"F3.wireOp",EDGE,"E27")}),1.0]])]});
            var Q2;
            {var subQ0=sQuery(id+"F3.wireOp",EDGE,"E25.MirrorCS");Q2=makeQuery(id+"F3.imprint","IMPRINT",FACE,{"disambiguationData":[TD([[makeQuery(id+"F3.imprint","IMPRINT",EDGE,{"derivedFrom":subQ0}),1.0]])]});}
            var Q3;
            {var subQ0=sQuery(id+"F3.wireOp",EDGE,"E23");Q3=makeQuery(id+"F3.imprint","IMPRINT",FACE,{"disambiguationData":[TD([[makeQuery(id+"F3.imprint","IMPRINT",EDGE,{"derivedFrom":subQ0}),-1.0]])]});}
            var Q4;
            Q4=makeQuery(id+"F3.imprint","IMPRINT",FACE,{"disambiguationData":[TD([[makeQuery(id+"F3.imprint","IMPRINT",EDGE,{"derivedFrom":sQuery(id+"F3.wireOp",EDGE,"E28")}),-1.0]])]});
            extrude(context, id + "F23", {"entities" : qUnion([Q0, Q1, Q2, Q3, Q4]), "oppositeDirection" : true, "depth" : (getVariable(context, 'WT')) * mm});
        }
        {
            var Q0;
            Q0=makeQuery(id+"F5.imprint","IMPRINT",FACE,{"disambiguationData":[TD([[makeQuery(id+"F5.imprint","IMPRINT",EDGE,{"derivedFrom":sQuery(id+"F5.wireOp",EDGE,"E33.0")}),1.0]])]});
            var Q1;
            {var subQ0=sQuery(id+"F5.wireOp",EDGE,"E35.0");Q1=makeQuery(id+"F5.imprint","IMPRINT",FACE,{"disambiguationData":[TD([[makeQuery(id+"F5.imprint","IMPRINT",EDGE,{"derivedFrom":subQ0}),-1.0]])]});}
            var Q2;
            {var subQ0=sQuery(id+"F5.wireOp",EDGE,"E35.2");var subQ3=sQuery(id+"F5.wireOp",EDGE,"E34.0");var subQ4=makeQuery(id+"F5.imprint","INTERSECT",VERTEX,{"disambiguationData":[OD(0.0)],"derivedFrom":[subQ3,subQ0]});Q2=makeQuery(id+"F5.imprint","IMPRINT",FACE,{"disambiguationData":[TD([[makeQuery(id+"F5.imprint","IMPRINT",EDGE,{"disambiguationData":[TD([[subQ4,1.0]])],"derivedFrom":subQ3}),1.0]])]});}
            var Q3;
            {var subQ0=sQuery(id+"F5.wireOp",EDGE,"E35.4");Q3=makeQuery(id+"F5.imprint","IMPRINT",FACE,{"disambiguationData":[TD([[makeQuery(id+"F5.imprint","IMPRINT",EDGE,{"derivedFrom":subQ0}),-1.0]])]});}
            extrude(context, id + "F24", {"entities" : qUnion([Q0, Q1, Q2, Q3]), "depth" : (getVariable(context, 'WT')) * mm});
        }
        {
            var Q0;
            Q0=makeQuery(id+"F6.imprint","IMPRINT",FACE,{"disambiguationData":[TD([[makeQuery(id+"F6.imprint","IMPRINT",EDGE,{"derivedFrom":sQuery(id+"F6.wireOp",EDGE,"E36.2")}),1.0]])]});
            var Q1;
            {var subQ0=sQuery(id+"F6.wireOp",EDGE,"E39");Q1=makeQuery(id+"F6.imprint","IMPRINT",FACE,{"disambiguationData":[TD([[makeQuery(id+"F6.imprint","IMPRINT",EDGE,{"derivedFrom":subQ0}),-1.0]])]});}
            var Q2;
            {var subQ0=sQuery(id+"F6.wireOp",EDGE,"E42");Q2=makeQuery(id+"F6.imprint","IMPRINT",FACE,{"disambiguationData":[TD([[makeQuery(id+"F6.imprint","IMPRINT",EDGE,{"derivedFrom":subQ0}),-1.0]])]});}
            var Q3;
            {var subQ0=sQuery(id+"F6.wireOp",EDGE,"E43");Q3=makeQuery(id+"F6.imprint","IMPRINT",FACE,{"disambiguationData":[TD([[makeQuery(id+"F6.imprint","IMPRINT",EDGE,{"derivedFrom":subQ0}),1.0]])]});}
            var Q4;
            {var subQ0=sQuery(id+"F6.wireOp",EDGE,"E45.1.1.0");Q4=makeQuery(id+"F6.imprint","IMPRINT",FACE,{"disambiguationData":[TD([[makeQuery(id+"F6.imprint","IMPRINT",EDGE,{"derivedFrom":subQ0}),-1.0]])]});}
            var Q5;
            {var subQ0=sQuery(id+"F6.wireOp",EDGE,"E45.1.0.0");Q5=makeQuery(id+"F6.imprint","IMPRINT",FACE,{"disambiguationData":[TD([[makeQuery(id+"F6.imprint","IMPRINT",EDGE,{"derivedFrom":subQ0}),-1.0]])]});}
            var Q6;
            {var subQ0=sQuery(id+"F6.wireOp",EDGE,"E45.3.0.0");Q6=makeQuery(id+"F6.imprint","IMPRINT",FACE,{"disambiguationData":[TD([[makeQuery(id+"F6.imprint","IMPRINT",EDGE,{"derivedFrom":subQ0}),-1.0]])]});}
            var Q7;
            {var subQ0=sQuery(id+"F6.wireOp",EDGE,"E45.3.1.0");Q7=makeQuery(id+"F6.imprint","IMPRINT",FACE,{"disambiguationData":[TD([[makeQuery(id+"F6.imprint","IMPRINT",EDGE,{"derivedFrom":subQ0}),-1.0]])]});}
            var Q8;
            {var subQ0=sQuery(id+"F6.wireOp",EDGE,"E45.5.0.0");Q8=makeQuery(id+"F6.imprint","IMPRINT",FACE,{"disambiguationData":[TD([[makeQuery(id+"F6.imprint","IMPRINT",EDGE,{"derivedFrom":subQ0}),-1.0]])]});}
            var Q9;
            {var subQ0=sQuery(id+"F6.wireOp",EDGE,"E45.7.0.0");Q9=makeQuery(id+"F6.imprint","IMPRINT",FACE,{"disambiguationData":[TD([[makeQuery(id+"F6.imprint","IMPRINT",EDGE,{"derivedFrom":subQ0}),-1.0]])]});}
            var Q10;
            {var subQ0=sQuery(id+"F6.wireOp",EDGE,"E45.7.1.0");Q10=makeQuery(id+"F6.imprint","IMPRINT",FACE,{"disambiguationData":[TD([[makeQuery(id+"F6.imprint","IMPRINT",EDGE,{"derivedFrom":subQ0}),-1.0]])]});}
            var Q11;
            {var subQ0=sQuery(id+"F6.wireOp",EDGE,"E45.5.1.0");Q11=makeQuery(id+"F6.imprint","IMPRINT",FACE,{"disambiguationData":[TD([[makeQuery(id+"F6.imprint","IMPRINT",EDGE,{"derivedFrom":subQ0}),-1.0]])]});}
            var Q12;
            {var subQ0=sQuery(id+"F6.wireOp",EDGE,"E41");Q12=makeQuery(id+"F6.imprint","IMPRINT",FACE,{"disambiguationData":[TD([[makeQuery(id+"F6.imprint","IMPRINT",EDGE,{"derivedFrom":subQ0}),-1.0]])]});}
            var Q13;
            {var subQ0=sQuery(id+"F6.wireOp",EDGE,"E45.9.1.0");Q13=makeQuery(id+"F6.imprint","IMPRINT",FACE,{"disambiguationData":[TD([[makeQuery(id+"F6.imprint","IMPRINT",EDGE,{"derivedFrom":subQ0}),-1.0]])]});}
            var Q14;
            {var subQ0=sQuery(id+"F6.wireOp",EDGE,"E45.11.1.0");Q14=makeQuery(id+"F6.imprint","IMPRINT",FACE,{"disambiguationData":[TD([[makeQuery(id+"F6.imprint","IMPRINT",EDGE,{"derivedFrom":subQ0}),-1.0]])]});}
            var Q15;
            {var subQ0=sQuery(id+"F6.wireOp",EDGE,"E45.11.0.0");Q15=makeQuery(id+"F6.imprint","IMPRINT",FACE,{"disambiguationData":[TD([[makeQuery(id+"F6.imprint","IMPRINT",EDGE,{"derivedFrom":subQ0}),-1.0]])]});}
            var Q16;
            {var subQ0=sQuery(id+"F6.wireOp",EDGE,"E45.13.0.0");Q16=makeQuery(id+"F6.imprint","IMPRINT",FACE,{"disambiguationData":[TD([[makeQuery(id+"F6.imprint","IMPRINT",EDGE,{"derivedFrom":subQ0}),-1.0]])]});}
            var Q17;
            {var subQ0=sQuery(id+"F6.wireOp",EDGE,"E45.13.1.0");Q17=makeQuery(id+"F6.imprint","IMPRINT",FACE,{"disambiguationData":[TD([[makeQuery(id+"F6.imprint","IMPRINT",EDGE,{"derivedFrom":subQ0}),-1.0]])]});}
            var Q18;
            {var subQ0=sQuery(id+"F6.wireOp",EDGE,"E45.15.1.0");Q18=makeQuery(id+"F6.imprint","IMPRINT",FACE,{"disambiguationData":[TD([[makeQuery(id+"F6.imprint","IMPRINT",EDGE,{"derivedFrom":subQ0}),-1.0]])]});}
            var Q19;
            {var subQ0=sQuery(id+"F6.wireOp",EDGE,"E45.15.0.0");Q19=makeQuery(id+"F6.imprint","IMPRINT",FACE,{"disambiguationData":[TD([[makeQuery(id+"F6.imprint","IMPRINT",EDGE,{"derivedFrom":subQ0}),-1.0]])]});}
            var Q20;
            {var subQ0=sQuery(id+"F6.wireOp",EDGE,"E45.17.0.0");Q20=makeQuery(id+"F6.imprint","IMPRINT",FACE,{"disambiguationData":[TD([[makeQuery(id+"F6.imprint","IMPRINT",EDGE,{"derivedFrom":subQ0}),-1.0]])]});}
            var Q21;
            {var subQ0=sQuery(id+"F6.wireOp",EDGE,"E45.17.1.0");Q21=makeQuery(id+"F6.imprint","IMPRINT",FACE,{"disambiguationData":[TD([[makeQuery(id+"F6.imprint","IMPRINT",EDGE,{"derivedFrom":subQ0}),-1.0]])]});}
            var Q22;
            {var subQ2=sQuery(id+"F6.wireOp",EDGE,"E48.MirrorCS");Q22=makeQuery(id+"F6.imprint","IMPRINT",FACE,{"disambiguationData":[TD([[makeQuery(id+"F6.imprint","IMPRINT",EDGE,{"derivedFrom":subQ2}),1.0]])]});}
            var Q23;
            {var subQ0=sQuery(id+"F6.wireOp",EDGE,"E46.MirrorCS");Q23=makeQuery(id+"F6.imprint","IMPRINT",FACE,{"disambiguationData":[TD([[makeQuery(id+"F6.imprint","IMPRINT",EDGE,{"derivedFrom":subQ0}),-1.0]])]});}
            var Q24;
            Q24=makeQuery(id+"F6.imprint","IMPRINT",FACE,{"disambiguationData":[TD([[makeQuery(id+"F6.imprint","IMPRINT",EDGE,{"derivedFrom":sQuery(id+"F6.wireOp",EDGE,"vp2r96jn-OqHV-6H2P-WP5b-Mt4CMppLmauR")}),1.0]])]});
            var Q25;
            Q25=makeQuery(id+"F6.imprint","IMPRINT",FACE,{"disambiguationData":[TD([[makeQuery(id+"F6.imprint","IMPRINT",EDGE,{"derivedFrom":sQuery(id+"F6.wireOp",EDGE,"E57.MirrorC")}),-1.0]])]});
            var Q26;
            Q26=makeQuery(id+"F6.imprint","IMPRINT",FACE,{"disambiguationData":[TD([[makeQuery(id+"F6.imprint","IMPRINT",EDGE,{"derivedFrom":sQuery(id+"F6.wireOp",EDGE,"E37.0")}),1.0]])]});
            extrude(context, id + "F25", {"entities" : qUnion([Q0, Q1, Q2, Q3, Q4, Q5, Q6, Q7, Q8, Q9, Q10, Q11, Q12, Q13, Q14, Q15, Q16, Q17, Q18, Q19, Q20, Q21, Q22, Q23, Q24, Q25, Q26]), "oppositeDirection" : true, "depth" : (getVariable(context, 'WT')) * mm});
        }
        {
            var Q0;
            Q0=makeQuery(id+"F8.imprint","IMPRINT",FACE,{"disambiguationData":[TD([[makeQuery(id+"F8.imprint","IMPRINT",EDGE,{"derivedFrom":sQuery(id+"F8.wireOp",EDGE,"E59.0")}),-1.0]])]});
            extrude(context, id + "F26", {"entities" : qUnion([Q0]), "depth" : (getVariable(context, 'WT')) * mm});
        }
        {
            var Q0;
            Q0=makeQuery(id+"F10.imprint","IMPRINT",FACE,{"disambiguationData":[TD([[makeQuery(id+"F10.imprint","IMPRINT",EDGE,{"derivedFrom":sQuery(id+"F10.wireOp",EDGE,"E63.0")}),-1.0]])]});
            extrude(context, id + "F27", {"entities" : qUnion([Q0]), "oppositeDirection" : true, "depth" : (getVariable(context, 'WT')) * mm});
        }
        {
            var Q0;
            Q0=makeQuery(id+"F12.imprint","IMPRINT",FACE,{"disambiguationData":[TD([[makeQuery(id+"F12.imprint","IMPRINT",EDGE,{"derivedFrom":sQuery(id+"F12.wireOp",EDGE,"E65.0")}),-1.0]])]});
            extrude(context, id + "F28", {"entities" : qUnion([Q0]), "oppositeDirection" : true, "depth" : (getVariable(context, 'WT')) * mm});
        }
        {
            var Q0;
            Q0=makeQuery(id+"F14.imprint","IMPRINT",FACE,{"disambiguationData":[TD([[makeQuery(id+"F14.imprint","IMPRINT",EDGE,{"derivedFrom":sQuery(id+"F14.wireOp",EDGE,"E69.0")}),-1.0]])]});
            extrude(context, id + "F29", {"entities" : qUnion([Q0]), "depth" : (getVariable(context, 'WT')) * mm});
        }
        {
            var Q0;
            {var subQ0=sQuery(id+"F16.wireOp",EDGE,"E75.1");Q0=makeQuery(id+"F16.imprint","IMPRINT",FACE,{"disambiguationData":[TD([[makeQuery(id+"F16.imprint","IMPRINT",EDGE,{"derivedFrom":subQ0}),-1.0]])]});}
            var Q1;
            {var subQ1=sQuery(id+"F16.wireOp",EDGE,"E75.0");Q1=makeQuery(id+"F16.imprint","IMPRINT",FACE,{"disambiguationData":[TD([[makeQuery(id+"F16.imprint","IMPRINT",EDGE,{"derivedFrom":subQ1}),-1.0]])]});}
            var Q2;
            {var subQ1=sQuery(id+"F16.wireOp",EDGE,"E75.3");Q2=makeQuery(id+"F16.imprint","IMPRINT",FACE,{"disambiguationData":[TD([[makeQuery(id+"F16.imprint","IMPRINT",EDGE,{"derivedFrom":subQ1}),1.0]])]});}
            var Q3;
            {var subQ0=sQuery(id+"F16.wireOp",EDGE,"E78.2");Q3=makeQuery(id+"F16.imprint","IMPRINT",FACE,{"disambiguationData":[TD([[makeQuery(id+"F16.imprint","IMPRINT",EDGE,{"derivedFrom":subQ0}),-1.0]])]});}
            var Q4;
            {var subQ0=sQuery(id+"F16.wireOp",EDGE,"E78.3");Q4=makeQuery(id+"F16.imprint","IMPRINT",FACE,{"disambiguationData":[TD([[makeQuery(id+"F16.imprint","IMPRINT",EDGE,{"derivedFrom":subQ0}),-1.0]])]});}
            var Q5;
            {var subQ0=sQuery(id+"F16.wireOp",EDGE,"E78.6");Q5=makeQuery(id+"F16.imprint","IMPRINT",FACE,{"disambiguationData":[TD([[makeQuery(id+"F16.imprint","IMPRINT",EDGE,{"derivedFrom":subQ0}),-1.0]])]});}
            var Q6;
            {var subQ0=sQuery(id+"F16.wireOp",EDGE,"E78.7");Q6=makeQuery(id+"F16.imprint","IMPRINT",FACE,{"disambiguationData":[TD([[makeQuery(id+"F16.imprint","IMPRINT",EDGE,{"derivedFrom":subQ0}),-1.0]])]});}
            var Q7;
            {var subQ0=sQuery(id+"F16.wireOp",EDGE,"E78.10");Q7=makeQuery(id+"F16.imprint","IMPRINT",FACE,{"disambiguationData":[TD([[makeQuery(id+"F16.imprint","IMPRINT",EDGE,{"derivedFrom":subQ0}),-1.0]])]});}
            var Q8;
            {var subQ0=sQuery(id+"F16.wireOp",EDGE,"E78.11");Q8=makeQuery(id+"F16.imprint","IMPRINT",FACE,{"disambiguationData":[TD([[makeQuery(id+"F16.imprint","IMPRINT",EDGE,{"derivedFrom":subQ0}),-1.0]])]});}
            var Q9;
            {var subQ0=sQuery(id+"F16.wireOp",EDGE,"E78.14");Q9=makeQuery(id+"F16.imprint","IMPRINT",FACE,{"disambiguationData":[TD([[makeQuery(id+"F16.imprint","IMPRINT",EDGE,{"derivedFrom":subQ0}),-1.0]])]});}
            var Q10;
            {var subQ0=sQuery(id+"F16.wireOp",EDGE,"E78.15");Q10=makeQuery(id+"F16.imprint","IMPRINT",FACE,{"disambiguationData":[TD([[makeQuery(id+"F16.imprint","IMPRINT",EDGE,{"derivedFrom":subQ0}),-1.0]])]});}
            var Q11;
            {var subQ0=sQuery(id+"F16.wireOp",EDGE,"E78.18");Q11=makeQuery(id+"F16.imprint","IMPRINT",FACE,{"disambiguationData":[TD([[makeQuery(id+"F16.imprint","IMPRINT",EDGE,{"derivedFrom":subQ0}),-1.0]])]});}
            var Q12;
            {var subQ0=sQuery(id+"F16.wireOp",EDGE,"E78.19");Q12=makeQuery(id+"F16.imprint","IMPRINT",FACE,{"disambiguationData":[TD([[makeQuery(id+"F16.imprint","IMPRINT",EDGE,{"derivedFrom":subQ0}),-1.0]])]});}
            var Q13;
            {var subQ0=sQuery(id+"F16.wireOp",EDGE,"E79.0");Q13=makeQuery(id+"F16.imprint","IMPRINT",FACE,{"disambiguationData":[TD([[makeQuery(id+"F16.imprint","IMPRINT",EDGE,{"derivedFrom":subQ0}),-1.0]])]});}
            var Q14;
            {var subQ0=sQuery(id+"F16.wireOp",EDGE,"E79.1");Q14=makeQuery(id+"F16.imprint","IMPRINT",FACE,{"disambiguationData":[TD([[makeQuery(id+"F16.imprint","IMPRINT",EDGE,{"derivedFrom":subQ0}),-1.0]])]});}
            var Q15;
            {var subQ0=sQuery(id+"F16.wireOp",EDGE,"E79.5");Q15=makeQuery(id+"F16.imprint","IMPRINT",FACE,{"disambiguationData":[TD([[makeQuery(id+"F16.imprint","IMPRINT",EDGE,{"derivedFrom":subQ0}),-1.0]])]});}
            var Q16;
            {var subQ0=sQuery(id+"F16.wireOp",EDGE,"E79.4");Q16=makeQuery(id+"F16.imprint","IMPRINT",FACE,{"disambiguationData":[TD([[makeQuery(id+"F16.imprint","IMPRINT",EDGE,{"derivedFrom":subQ0}),-1.0]])]});}
            var Q17;
            {var subQ0=sQuery(id+"F16.wireOp",EDGE,"E80.0");Q17=makeQuery(id+"F16.imprint","IMPRINT",FACE,{"disambiguationData":[TD([[makeQuery(id+"F16.imprint","IMPRINT",EDGE,{"derivedFrom":subQ0}),-1.0]])]});}
            var Q18;
            {var subQ0=sQuery(id+"F16.wireOp",EDGE,"E80.1");Q18=makeQuery(id+"F16.imprint","IMPRINT",FACE,{"disambiguationData":[TD([[makeQuery(id+"F16.imprint","IMPRINT",EDGE,{"derivedFrom":subQ0}),-1.0]])]});}
            var Q19;
            {var subQ0=sQuery(id+"F16.wireOp",EDGE,"E80.5");Q19=makeQuery(id+"F16.imprint","IMPRINT",FACE,{"disambiguationData":[TD([[makeQuery(id+"F16.imprint","IMPRINT",EDGE,{"derivedFrom":subQ0}),-1.0]])]});}
            var Q20;
            {var subQ0=sQuery(id+"F16.wireOp",EDGE,"E80.4");Q20=makeQuery(id+"F16.imprint","IMPRINT",FACE,{"disambiguationData":[TD([[makeQuery(id+"F16.imprint","IMPRINT",EDGE,{"derivedFrom":subQ0}),-1.0]])]});}
            var Q21;
            {var subQ0=sQuery(id+"F16.wireOp",EDGE,"E80.9");Q21=makeQuery(id+"F16.imprint","IMPRINT",FACE,{"disambiguationData":[TD([[makeQuery(id+"F16.imprint","IMPRINT",EDGE,{"derivedFrom":subQ0}),-1.0]])]});}
            var Q22;
            {var subQ0=sQuery(id+"F16.wireOp",EDGE,"E80.10");Q22=makeQuery(id+"F16.imprint","IMPRINT",FACE,{"disambiguationData":[TD([[makeQuery(id+"F16.imprint","IMPRINT",EDGE,{"derivedFrom":subQ0}),1.0]])]});}
            var Q23;
            {var subQ11=sQuery(id+"F16.wireOp",EDGE,"E74.0");var subQ19=makeQuery(id+"F16.imprint","INTERSECT",VERTEX,{"derivedFrom":[subQ11,sQuery(id+"F16.wireOp",EDGE,"E75.1")]});Q23=makeQuery(id+"F16.imprint","IMPRINT",FACE,{"disambiguationData":[TD([[makeQuery(id+"F16.imprint","IMPRINT",EDGE,{"disambiguationData":[TD([[subQ19,-1.0]])],"derivedFrom":subQ11}),1.0]])]});}
            extrude(context, id + "F30", {"entities" : qUnion([Q0, Q1, Q2, Q3, Q4, Q5, Q6, Q7, Q8, Q9, Q10, Q11, Q12, Q13, Q14, Q15, Q16, Q17, Q18, Q19, Q20, Q21, Q22, Q23]), "oppositeDirection" : true, "depth" : (getVariable(context, 'WT')) * mm});
        }
        {
            var Q0;
            Q0=makeQuery(id+"F30.opExtrude","CAP_FACE",FACE,{"disambiguationData":[OSD([sQuery(id+"F16.wireOp",EDGE,"E73.0"),sQuery(id+"F16.wireOp",EDGE,"E73.1"),sQuery(id+"F16.wireOp",EDGE,"E73.2"),sQuery(id+"F16.wireOp",EDGE,"E73.3"),sQuery(id+"F16.wireOp",EDGE,"E74.0"),sQuery(id+"F16.wireOp",EDGE,"E75.0"),sQuery(id+"F16.wireOp",EDGE,"E75.1"),sQuery(id+"F16.wireOp",EDGE,"E75.2"),sQuery(id+"F16.wireOp",EDGE,"E75.3"),sQuery(id+"F16.wireOp",EDGE,"E76.0"),sQuery(id+"F16.wireOp",EDGE,"E77.0"),sQuery(id+"F16.wireOp",EDGE,"E78.0"),sQuery(id+"F16.wireOp",EDGE,"E78.1"),sQuery(id+"F16.wireOp",EDGE,"E78.2"),sQuery(id+"F16.wireOp",EDGE,"E78.3"),sQuery(id+"F16.wireOp",EDGE,"E78.4"),sQuery(id+"F16.wireOp",EDGE,"E78.5"),sQuery(id+"F16.wireOp",EDGE,"E78.6"),sQuery(id+"F16.wireOp",EDGE,"E78.7"),sQuery(id+"F16.wireOp",EDGE,"E78.8"),sQuery(id+"F16.wireOp",EDGE,"E78.9"),sQuery(id+"F16.wireOp",EDGE,"E78.10"),sQuery(id+"F16.wireOp",EDGE,"E78.11"),sQuery(id+"F16.wireOp",EDGE,"E78.12"),sQuery(id+"F16.wireOp",EDGE,"E78.13"),sQuery(id+"F16.wireOp",EDGE,"E78.14"),sQuery(id+"F16.wireOp",EDGE,"E78.15"),sQuery(id+"F16.wireOp",EDGE,"E78.16"),sQuery(id+"F16.wireOp",EDGE,"E78.17"),sQuery(id+"F16.wireOp",EDGE,"E78.18"),sQuery(id+"F16.wireOp",EDGE,"E78.19"),sQuery(id+"F16.wireOp",EDGE,"E78.20"),sQuery(id+"F16.wireOp",EDGE,"E78.21"),sQuery(id+"F16.wireOp",EDGE,"E79.0"),sQuery(id+"F16.wireOp",EDGE,"E79.1"),sQuery(id+"F16.wireOp",EDGE,"E79.2"),sQuery(id+"F16.wireOp",EDGE,"E79.3"),sQuery(id+"F16.wireOp",EDGE,"E79.4"),sQuery(id+"F16.wireOp",EDGE,"E79.5"),sQuery(id+"F16.wireOp",EDGE,"E79.6"),sQuery(id+"F16.wireOp",EDGE,"E79.7"),sQuery(id+"F16.wireOp",EDGE,"E80.0"),sQuery(id+"F16.wireOp",EDGE,"E80.1"),sQuery(id+"F16.wireOp",EDGE,"E80.2"),sQuery(id+"F16.wireOp",EDGE,"E80.3"),sQuery(id+"F16.wireOp",EDGE,"E80.4"),sQuery(id+"F16.wireOp",EDGE,"E80.5"),sQuery(id+"F16.wireOp",EDGE,"E80.6"),sQuery(id+"F16.wireOp",EDGE,"E80.7"),sQuery(id+"F16.wireOp",EDGE,"E80.8"),sQuery(id+"F16.wireOp",EDGE,"E80.9"),sQuery(id+"F16.wireOp",EDGE,"E80.10"),sQuery(id+"F16.wireOp",EDGE,"E80.11"),sQuery(id+"F16.wireOp",EDGE,"E81.0")])],"isStart":true});
            extrude(context, id + "F31", {"entities" : qUnion([Q0]), "operationType" : NewBodyOperationType.REMOVE, "oppositeDirection" : true, "depth" : (getVariable(context, 'WT')) * mm});
        }
        {
            var Q0;
            Q0=makeQuery(id+"F25.opExtrude","CAP_FACE",FACE,{"disambiguationData":[OSD([sQuery(id+"F6.wireOp",EDGE,"E36.0"),sQuery(id+"F6.wireOp",EDGE,"E36.1"),sQuery(id+"F6.wireOp",EDGE,"E36.2"),sQuery(id+"F6.wireOp",EDGE,"E36.3"),sQuery(id+"F6.wireOp",EDGE,"E36.4"),sQuery(id+"F6.wireOp",EDGE,"E36.5"),sQuery(id+"F6.wireOp",EDGE,"E36.6"),sQuery(id+"F6.wireOp",EDGE,"E36.7"),sQuery(id+"F6.wireOp",EDGE,"E36.8"),sQuery(id+"F6.wireOp",EDGE,"E36.9"),sQuery(id+"F6.wireOp",EDGE,"E36.10"),sQuery(id+"F6.wireOp",EDGE,"E36.11"),sQuery(id+"F6.wireOp",EDGE,"E38"),sQuery(id+"F6.wireOp",EDGE,"dPC2vHzn-LRmz-Www3-GGar-EtB5FnVSiI05"),sQuery(id+"F6.wireOp",EDGE,"vp2r96jn-OqHV-6H2P-WP5b-Mt4CMppLmauR"),sQuery(id+"F6.wireOp",EDGE,"E39"),sQuery(id+"F6.wireOp",EDGE,"E40"),sQuery(id+"F6.wireOp",EDGE,"E42"),sQuery(id+"F6.wireOp",EDGE,"E43"),sQuery(id+"F6.wireOp",EDGE,"E44"),sQuery(id+"F6.wireOp",EDGE,"E45.0.1.0"),sQuery(id+"F6.wireOp",EDGE,"E45.1.0.0"),sQuery(id+"F6.wireOp",EDGE,"E45.1.1.0"),sQuery(id+"F6.wireOp",EDGE,"E45.2.0.0"),sQuery(id+"F6.wireOp",EDGE,"E45.2.1.0"),sQuery(id+"F6.wireOp",EDGE,"E45.3.0.0"),sQuery(id+"F6.wireOp",EDGE,"E45.3.1.0"),sQuery(id+"F6.wireOp",EDGE,"E45.4.0.0"),sQuery(id+"F6.wireOp",EDGE,"E45.4.1.0"),sQuery(id+"F6.wireOp",EDGE,"E45.5.0.0"),sQuery(id+"F6.wireOp",EDGE,"E45.5.1.0"),sQuery(id+"F6.wireOp",EDGE,"E45.6.0.0"),sQuery(id+"F6.wireOp",EDGE,"E45.6.1.0"),sQuery(id+"F6.wireOp",EDGE,"E45.7.0.0"),sQuery(id+"F6.wireOp",EDGE,"E45.7.1.0"),sQuery(id+"F6.wireOp",EDGE,"E45.8.0.0"),sQuery(id+"F6.wireOp",EDGE,"E45.8.1.0"),sQuery(id+"F6.wireOp",EDGE,"E41"),sQuery(id+"F6.wireOp",EDGE,"E45.9.1.0"),sQuery(id+"F6.wireOp",EDGE,"E45.10.0.0"),sQuery(id+"F6.wireOp",EDGE,"E45.10.1.0"),sQuery(id+"F6.wireOp",EDGE,"E45.11.0.0"),sQuery(id+"F6.wireOp",EDGE,"E45.11.1.0"),sQuery(id+"F6.wireOp",EDGE,"E45.12.0.0"),sQuery(id+"F6.wireOp",EDGE,"E45.12.1.0"),sQuery(id+"F6.wireOp",EDGE,"E45.13.0.0"),sQuery(id+"F6.wireOp",EDGE,"E45.13.1.0"),sQuery(id+"F6.wireOp",EDGE,"E45.14.0.0"),sQuery(id+"F6.wireOp",EDGE,"E45.14.1.0"),sQuery(id+"F6.wireOp",EDGE,"E45.15.0.0"),sQuery(id+"F6.wireOp",EDGE,"E45.15.1.0"),sQuery(id+"F6.wireOp",EDGE,"E45.16.0.0"),sQuery(id+"F6.wireOp",EDGE,"E45.16.1.0"),sQuery(id+"F6.wireOp",EDGE,"E45.17.0.0"),sQuery(id+"F6.wireOp",EDGE,"E45.17.1.0"),sQuery(id+"F6.wireOp",EDGE,"E45.18.0.0"),sQuery(id+"F6.wireOp",EDGE,"E45.18.1.0"),sQuery(id+"F6.wireOp",EDGE,"E46.MirrorCS"),sQuery(id+"F6.wireOp",EDGE,"E47.MirrorCS"),sQuery(id+"F6.wireOp",EDGE,"E48.MirrorCS"),sQuery(id+"F6.wireOp",EDGE,"E49.MirrorCS")])],"isStart":false});
            extrude(context, id + "F32", {"entities" : qUnion([Q0]), "operationType" : NewBodyOperationType.REMOVE, "oppositeDirection" : true, "depth" : (getVariable(context, 'WT')) * mm});
        }
        {
            var Q0;
            Q0=makeQuery(id+"F29.opExtrude","CAP_FACE",FACE,{"disambiguationData":[OSD([sQuery(id+"F14.wireOp",EDGE,"E69.0"),sQuery(id+"F14.wireOp",EDGE,"E70.0"),sQuery(id+"F14.wireOp",EDGE,"E71.0"),sQuery(id+"F14.wireOp",EDGE,"E72.0")])],"isStart":true});
            extrude(context, id + "F33", {"entities" : qUnion([Q0]), "operationType" : NewBodyOperationType.REMOVE, "oppositeDirection" : true, "depth" : (getVariable(context, 'WT')) * mm});
        }
        {
            var Q0;
            Q0=makeQuery(id+"F28.opExtrude","CAP_FACE",FACE,{"disambiguationData":[OSD([sQuery(id+"F12.wireOp",EDGE,"E65.0"),sQuery(id+"F12.wireOp",EDGE,"E66.0"),sQuery(id+"F12.wireOp",EDGE,"E67"),sQuery(id+"F12.wireOp",EDGE,"E68")])],"isStart":true});
            extrude(context, id + "F34", {"entities" : qUnion([Q0]), "operationType" : NewBodyOperationType.REMOVE, "oppositeDirection" : true, "depth" : (getVariable(context, 'WT')) * mm});
        }
        {
            var Q0;
            Q0=makeQuery(id+"F6.imprint","IMPRINT",FACE,{"disambiguationData":[TD([[makeQuery(id+"F6.imprint","IMPRINT",EDGE,{"derivedFrom":sQuery(id+"F6.wireOp",EDGE,"E37.0")}),1.0]])]});
            var Q1;
            Q1=makeQuery(id+"F6.imprint","IMPRINT",FACE,{"disambiguationData":[TD([[makeQuery(id+"F6.imprint","IMPRINT",EDGE,{"derivedFrom":sQuery(id+"F6.wireOp",EDGE,"vp2r96jn-OqHV-6H2P-WP5b-Mt4CMppLmauR")}),1.0]])]});
            extrude(context, id + "F35", {"entities" : qUnion([Q0, Q1]), "depth" : (getVariable(context, 'WT')) * mm});
        }
        {
            var Q0;
            Q0=makeQuery(id+"F18.imprint","IMPRINT",FACE,{"disambiguationData":[TD([[makeQuery(id+"F18.imprint","IMPRINT",EDGE,{"derivedFrom":sQuery(id+"F18.wireOp",EDGE,"E82.0")}),-1.0]])]});
            extrude(context, id + "F36", {"entities" : qUnion([Q0]), "depth" : (getVariable(context, 'WT')) * mm});
        }
        {
            var Q0;
            {var subQ1=sQuery(id+"F18.wireOp",EDGE,"E103.MirrorCS");Q0=makeQuery(id+"F18.imprint","IMPRINT",FACE,{"disambiguationData":[TD([[makeQuery(id+"F18.imprint","IMPRINT",EDGE,{"derivedFrom":subQ1}),1.0]])]});}
            var Q1;
            Q1=makeQuery(id+"F18.imprint","IMPRINT",FACE,{"disambiguationData":[TD([[makeQuery(id+"F18.imprint","IMPRINT",EDGE,{"derivedFrom":sQuery(id+"F18.wireOp",EDGE,"E82.0")}),-1.0]])]});
            extrude(context, id + "F37", {"entities" : qUnion([Q0, Q1]), "depth" : (getVariable(context, 'WT')) * mm});
        }
        {
            var Q0;
            Q0=makeQuery(id+"F37.opExtrude","CAP_FACE",FACE,{"disambiguationData":[OSD([sQuery(id+"F18.wireOp",EDGE,"E84.0"),sQuery(id+"F18.wireOp",EDGE,"E85.0"),sQuery(id+"F18.wireOp",EDGE,"E103.MirrorCS"),sQuery(id+"F18.wireOp",EDGE,"E105.MirrorCS"),sQuery(id+"F18.wireOp",EDGE,"E106.MirrorCS"),sQuery(id+"F18.wireOp",EDGE,"E107.MirrorCS"),sQuery(id+"F18.wireOp",EDGE,"E108.MirrorCS"),sQuery(id+"F18.wireOp",EDGE,"E109.MirrorCS"),sQuery(id+"F18.wireOp",EDGE,"E102.MirrorCS"),sQuery(id+"F18.wireOp",EDGE,"E110.0"),sQuery(id+"F18.wireOp",EDGE,"E111.trimOffspring")])],"isStart":false});
            var Q1;
            Q1=makeQuery(id+"F36.opExtrude","CAP_FACE",FACE,{"disambiguationData":[OSD([sQuery(id+"F18.wireOp",EDGE,"E82.0"),sQuery(id+"F18.wireOp",EDGE,"E84.0"),sQuery(id+"F18.wireOp",EDGE,"E85.0"),sQuery(id+"F18.wireOp",EDGE,"E86"),sQuery(id+"F18.wireOp",EDGE,"E87"),sQuery(id+"F18.wireOp",EDGE,"E89"),sQuery(id+"F18.wireOp",EDGE,"E91.MirrorCS"),sQuery(id+"F18.wireOp",EDGE,"E92.MirrorCS"),sQuery(id+"F18.wireOp",EDGE,"E93.MirrorCS"),sQuery(id+"F18.wireOp",EDGE,"E98.trimOffspring"),sQuery(id+"F18.wireOp",EDGE,"E99.trimOffspring")])],"isStart":false});
            extrude(context, id + "F38", {"entities" : qUnion([Q0, Q1]), "operationType" : NewBodyOperationType.REMOVE, "oppositeDirection" : true, "depth" : (getVariable(context, 'WT')) * mm});
        }
        {
            var Q0;
            {var subQ5=sQuery(id+"F3.wireOp",EDGE,"E31");Q0=makeQuery(id+"F3.imprint","IMPRINT",FACE,{"disambiguationData":[TD([[makeQuery(id+"F3.imprint","IMPRINT",EDGE,{"derivedFrom":subQ5}),1.0]])]});}
            var Q1;
            Q1=makeQuery(id+"F3.imprint","IMPRINT",FACE,{"disambiguationData":[TD([[makeQuery(id+"F3.imprint","IMPRINT",EDGE,{"derivedFrom":sQuery(id+"F3.wireOp",EDGE,"E28")}),-1.0]])]});
            var Q2;
            {var subQ5=sQuery(id+"F3.wireOp",EDGE,"E32.MirrorCS");Q2=makeQuery(id+"F3.imprint","IMPRINT",FACE,{"disambiguationData":[TD([[makeQuery(id+"F3.imprint","IMPRINT",EDGE,{"derivedFrom":subQ5}),-1.0]])]});}
            extrude(context, id + "F39", {"entities" : qUnion([Q0, Q1, Q2]), "depth" : (getVariable(context, 'WT')) * mm});
        }
        {
            var Q0;
            Q0=makeQuery(id+"F21.imprint","IMPRINT",FACE,{"disambiguationData":[TD([[makeQuery(id+"F21.imprint","IMPRINT",EDGE,{"derivedFrom":sQuery(id+"F21.wireOp",EDGE,"E113.0")}),1.0]])]});
            extrude(context, id + "F40", {"entities" : qUnion([Q0]), "depth" : (getVariable(context, 'WT')) * mm});
        }
        {
            var Q0;
            {var subQ0=sQuery(id+"F21.wireOp",EDGE,"E122.1.0");var subQ1=sQuery(id+"F21.wireOp",EDGE,"E115");var subQ2=makeQuery(id+"F21.imprint","INTERSECT",VERTEX,{"derivedFrom":[subQ1,subQ0]});Q0=makeQuery(id+"F21.imprint","IMPRINT",FACE,{"disambiguationData":[TD([[makeQuery(id+"F21.imprint","IMPRINT",EDGE,{"disambiguationData":[TD([[subQ2,-1.0]])],"derivedFrom":subQ1}),1.0]])]});}
            var Q1;
            {var subQ0=sQuery(id+"F21.wireOp",EDGE,"E122.2.0");var subQ1=sQuery(id+"F21.wireOp",EDGE,"E114");var subQ2=makeQuery(id+"F21.imprint","INTERSECT",VERTEX,{"derivedFrom":[subQ1,subQ0]});Q1=makeQuery(id+"F21.imprint","IMPRINT",FACE,{"disambiguationData":[TD([[makeQuery(id+"F21.imprint","IMPRINT",EDGE,{"disambiguationData":[TD([[subQ2,-1.0]])],"derivedFrom":subQ1}),1.0]])]});}
            var Q2;
            {var subQ0=sQuery(id+"F21.wireOp",EDGE,"E122.2.0");var subQ1=sQuery(id+"F21.wireOp",EDGE,"E115");var subQ2=makeQuery(id+"F21.imprint","INTERSECT",VERTEX,{"derivedFrom":[subQ1,subQ0]});Q2=makeQuery(id+"F21.imprint","IMPRINT",FACE,{"disambiguationData":[TD([[makeQuery(id+"F21.imprint","IMPRINT",EDGE,{"disambiguationData":[TD([[subQ2,-1.0]])],"derivedFrom":subQ1}),1.0]])]});}
            var Q3;
            {var subQ0=sQuery(id+"F21.wireOp",EDGE,"E122.34.0");var subQ1=sQuery(id+"F21.wireOp",EDGE,"E115");var subQ2=makeQuery(id+"F21.imprint","INTERSECT",VERTEX,{"derivedFrom":[subQ1,subQ0]});Q3=makeQuery(id+"F21.imprint","IMPRINT",FACE,{"disambiguationData":[TD([[makeQuery(id+"F21.imprint","IMPRINT",EDGE,{"disambiguationData":[TD([[subQ2,-1.0]])],"derivedFrom":subQ1}),1.0]])]});}
            var Q4;
            {var subQ0=sQuery(id+"F21.wireOp",EDGE,"E122.34.0");var subQ1=sQuery(id+"F21.wireOp",EDGE,"E114");var subQ2=makeQuery(id+"F21.imprint","INTERSECT",VERTEX,{"derivedFrom":[subQ1,subQ0]});Q4=makeQuery(id+"F21.imprint","IMPRINT",FACE,{"disambiguationData":[TD([[makeQuery(id+"F21.imprint","IMPRINT",EDGE,{"disambiguationData":[TD([[subQ2,-1.0]])],"derivedFrom":subQ1}),1.0]])]});}
            var Q5;
            {var subQ0=sQuery(id+"F21.wireOp",EDGE,"E122.33.0");var subQ1=sQuery(id+"F21.wireOp",EDGE,"E115");var subQ2=makeQuery(id+"F21.imprint","INTERSECT",VERTEX,{"derivedFrom":[subQ1,subQ0]});Q5=makeQuery(id+"F21.imprint","IMPRINT",FACE,{"disambiguationData":[TD([[makeQuery(id+"F21.imprint","IMPRINT",EDGE,{"disambiguationData":[TD([[subQ2,-1.0]])],"derivedFrom":subQ1}),1.0]])]});}
            var Q6;
            {var subQ0=sQuery(id+"F21.wireOp",EDGE,"E122.5.0");var subQ1=sQuery(id+"F21.wireOp",EDGE,"E115");var subQ2=makeQuery(id+"F21.imprint","INTERSECT",VERTEX,{"derivedFrom":[subQ1,subQ0]});Q6=makeQuery(id+"F21.imprint","IMPRINT",FACE,{"disambiguationData":[TD([[makeQuery(id+"F21.imprint","IMPRINT",EDGE,{"disambiguationData":[TD([[subQ2,-1.0]])],"derivedFrom":subQ1}),1.0]])]});}
            var Q7;
            {var subQ0=sQuery(id+"F21.wireOp",EDGE,"E122.6.0");var subQ1=sQuery(id+"F21.wireOp",EDGE,"E115");var subQ2=makeQuery(id+"F21.imprint","INTERSECT",VERTEX,{"derivedFrom":[subQ1,subQ0]});Q7=makeQuery(id+"F21.imprint","IMPRINT",FACE,{"disambiguationData":[TD([[makeQuery(id+"F21.imprint","IMPRINT",EDGE,{"disambiguationData":[TD([[subQ2,-1.0]])],"derivedFrom":subQ1}),1.0]])]});}
            var Q8;
            {var subQ0=sQuery(id+"F21.wireOp",EDGE,"E122.6.0");var subQ1=sQuery(id+"F21.wireOp",EDGE,"E114");var subQ2=makeQuery(id+"F21.imprint","INTERSECT",VERTEX,{"derivedFrom":[subQ1,subQ0]});Q8=makeQuery(id+"F21.imprint","IMPRINT",FACE,{"disambiguationData":[TD([[makeQuery(id+"F21.imprint","IMPRINT",EDGE,{"disambiguationData":[TD([[subQ2,-1.0]])],"derivedFrom":subQ1}),1.0]])]});}
            var Q9;
            {var subQ0=sQuery(id+"F21.wireOp",EDGE,"E122.9.0");var subQ1=sQuery(id+"F21.wireOp",EDGE,"E115");var subQ2=makeQuery(id+"F21.imprint","INTERSECT",VERTEX,{"derivedFrom":[subQ1,subQ0]});Q9=makeQuery(id+"F21.imprint","IMPRINT",FACE,{"disambiguationData":[TD([[makeQuery(id+"F21.imprint","IMPRINT",EDGE,{"disambiguationData":[TD([[subQ2,-1.0]])],"derivedFrom":subQ1}),1.0]])]});}
            var Q10;
            {var subQ0=sQuery(id+"F21.wireOp",EDGE,"E122.10.0");var subQ1=sQuery(id+"F21.wireOp",EDGE,"E115");var subQ2=makeQuery(id+"F21.imprint","INTERSECT",VERTEX,{"derivedFrom":[subQ1,subQ0]});Q10=makeQuery(id+"F21.imprint","IMPRINT",FACE,{"disambiguationData":[TD([[makeQuery(id+"F21.imprint","IMPRINT",EDGE,{"disambiguationData":[TD([[subQ2,-1.0]])],"derivedFrom":subQ1}),1.0]])]});}
            var Q11;
            {var subQ0=sQuery(id+"F21.wireOp",EDGE,"E122.10.0");var subQ1=sQuery(id+"F21.wireOp",EDGE,"E114");var subQ2=makeQuery(id+"F21.imprint","INTERSECT",VERTEX,{"derivedFrom":[subQ1,subQ0]});Q11=makeQuery(id+"F21.imprint","IMPRINT",FACE,{"disambiguationData":[TD([[makeQuery(id+"F21.imprint","IMPRINT",EDGE,{"disambiguationData":[TD([[subQ2,-1.0]])],"derivedFrom":subQ1}),1.0]])]});}
            var Q12;
            {var subQ0=sQuery(id+"F21.wireOp",EDGE,"E122.13.0");var subQ1=sQuery(id+"F21.wireOp",EDGE,"E115");var subQ2=makeQuery(id+"F21.imprint","INTERSECT",VERTEX,{"derivedFrom":[subQ1,subQ0]});Q12=makeQuery(id+"F21.imprint","IMPRINT",FACE,{"disambiguationData":[TD([[makeQuery(id+"F21.imprint","IMPRINT",EDGE,{"disambiguationData":[TD([[subQ2,-1.0]])],"derivedFrom":subQ1}),1.0]])]});}
            var Q13;
            {var subQ0=sQuery(id+"F21.wireOp",EDGE,"E122.14.0");var subQ1=sQuery(id+"F21.wireOp",EDGE,"E115");var subQ2=makeQuery(id+"F21.imprint","INTERSECT",VERTEX,{"derivedFrom":[subQ1,subQ0]});Q13=makeQuery(id+"F21.imprint","IMPRINT",FACE,{"disambiguationData":[TD([[makeQuery(id+"F21.imprint","IMPRINT",EDGE,{"disambiguationData":[TD([[subQ2,-1.0]])],"derivedFrom":subQ1}),1.0]])]});}
            var Q14;
            {var subQ0=sQuery(id+"F21.wireOp",EDGE,"E122.14.0");var subQ1=sQuery(id+"F21.wireOp",EDGE,"E114");var subQ2=makeQuery(id+"F21.imprint","INTERSECT",VERTEX,{"derivedFrom":[subQ1,subQ0]});Q14=makeQuery(id+"F21.imprint","IMPRINT",FACE,{"disambiguationData":[TD([[makeQuery(id+"F21.imprint","IMPRINT",EDGE,{"disambiguationData":[TD([[subQ2,-1.0]])],"derivedFrom":subQ1}),1.0]])]});}
            var Q15;
            {var subQ0=sQuery(id+"F21.wireOp",EDGE,"E122.17.0");var subQ1=sQuery(id+"F21.wireOp",EDGE,"E115");var subQ2=makeQuery(id+"F21.imprint","INTERSECT",VERTEX,{"derivedFrom":[subQ1,subQ0]});Q15=makeQuery(id+"F21.imprint","IMPRINT",FACE,{"disambiguationData":[TD([[makeQuery(id+"F21.imprint","IMPRINT",EDGE,{"disambiguationData":[TD([[subQ2,-1.0]])],"derivedFrom":subQ1}),1.0]])]});}
            var Q16;
            {var subQ0=sQuery(id+"F21.wireOp",EDGE,"E122.18.0");var subQ1=sQuery(id+"F21.wireOp",EDGE,"E115");var subQ2=makeQuery(id+"F21.imprint","INTERSECT",VERTEX,{"derivedFrom":[subQ1,subQ0]});Q16=makeQuery(id+"F21.imprint","IMPRINT",FACE,{"disambiguationData":[TD([[makeQuery(id+"F21.imprint","IMPRINT",EDGE,{"disambiguationData":[TD([[subQ2,-1.0]])],"derivedFrom":subQ1}),1.0]])]});}
            var Q17;
            {var subQ0=sQuery(id+"F21.wireOp",EDGE,"E122.18.0");var subQ1=sQuery(id+"F21.wireOp",EDGE,"E114");var subQ2=makeQuery(id+"F21.imprint","INTERSECT",VERTEX,{"derivedFrom":[subQ1,subQ0]});Q17=makeQuery(id+"F21.imprint","IMPRINT",FACE,{"disambiguationData":[TD([[makeQuery(id+"F21.imprint","IMPRINT",EDGE,{"disambiguationData":[TD([[subQ2,-1.0]])],"derivedFrom":subQ1}),1.0]])]});}
            var Q18;
            {var subQ0=sQuery(id+"F21.wireOp",EDGE,"E122.22.0");var subQ1=sQuery(id+"F21.wireOp",EDGE,"E115");var subQ2=makeQuery(id+"F21.imprint","INTERSECT",VERTEX,{"derivedFrom":[subQ1,subQ0]});Q18=makeQuery(id+"F21.imprint","IMPRINT",FACE,{"disambiguationData":[TD([[makeQuery(id+"F21.imprint","IMPRINT",EDGE,{"disambiguationData":[TD([[subQ2,-1.0]])],"derivedFrom":subQ1}),1.0]])]});}
            var Q19;
            {var subQ0=sQuery(id+"F21.wireOp",EDGE,"E122.22.0");var subQ1=sQuery(id+"F21.wireOp",EDGE,"E114");var subQ2=makeQuery(id+"F21.imprint","INTERSECT",VERTEX,{"derivedFrom":[subQ1,subQ0]});Q19=makeQuery(id+"F21.imprint","IMPRINT",FACE,{"disambiguationData":[TD([[makeQuery(id+"F21.imprint","IMPRINT",EDGE,{"disambiguationData":[TD([[subQ2,-1.0]])],"derivedFrom":subQ1}),1.0]])]});}
            var Q20;
            {var subQ0=sQuery(id+"F21.wireOp",EDGE,"E122.21.0");var subQ1=sQuery(id+"F21.wireOp",EDGE,"E115");var subQ2=makeQuery(id+"F21.imprint","INTERSECT",VERTEX,{"derivedFrom":[subQ1,subQ0]});Q20=makeQuery(id+"F21.imprint","IMPRINT",FACE,{"disambiguationData":[TD([[makeQuery(id+"F21.imprint","IMPRINT",EDGE,{"disambiguationData":[TD([[subQ2,-1.0]])],"derivedFrom":subQ1}),1.0]])]});}
            var Q21;
            {var subQ0=sQuery(id+"F21.wireOp",EDGE,"E122.26.0");var subQ1=sQuery(id+"F21.wireOp",EDGE,"E115");var subQ2=makeQuery(id+"F21.imprint","INTERSECT",VERTEX,{"derivedFrom":[subQ1,subQ0]});Q21=makeQuery(id+"F21.imprint","IMPRINT",FACE,{"disambiguationData":[TD([[makeQuery(id+"F21.imprint","IMPRINT",EDGE,{"disambiguationData":[TD([[subQ2,-1.0]])],"derivedFrom":subQ1}),1.0]])]});}
            var Q22;
            {var subQ0=sQuery(id+"F21.wireOp",EDGE,"E122.25.0");var subQ1=sQuery(id+"F21.wireOp",EDGE,"E115");var subQ2=makeQuery(id+"F21.imprint","INTERSECT",VERTEX,{"derivedFrom":[subQ1,subQ0]});Q22=makeQuery(id+"F21.imprint","IMPRINT",FACE,{"disambiguationData":[TD([[makeQuery(id+"F21.imprint","IMPRINT",EDGE,{"disambiguationData":[TD([[subQ2,-1.0]])],"derivedFrom":subQ1}),1.0]])]});}
            var Q23;
            {var subQ0=sQuery(id+"F21.wireOp",EDGE,"E122.26.0");var subQ1=sQuery(id+"F21.wireOp",EDGE,"E114");var subQ2=makeQuery(id+"F21.imprint","INTERSECT",VERTEX,{"derivedFrom":[subQ1,subQ0]});Q23=makeQuery(id+"F21.imprint","IMPRINT",FACE,{"disambiguationData":[TD([[makeQuery(id+"F21.imprint","IMPRINT",EDGE,{"disambiguationData":[TD([[subQ2,-1.0]])],"derivedFrom":subQ1}),1.0]])]});}
            var Q24;
            {var subQ0=sQuery(id+"F21.wireOp",EDGE,"E122.30.0");var subQ1=sQuery(id+"F21.wireOp",EDGE,"E115");var subQ2=makeQuery(id+"F21.imprint","INTERSECT",VERTEX,{"derivedFrom":[subQ1,subQ0]});Q24=makeQuery(id+"F21.imprint","IMPRINT",FACE,{"disambiguationData":[TD([[makeQuery(id+"F21.imprint","IMPRINT",EDGE,{"disambiguationData":[TD([[subQ2,-1.0]])],"derivedFrom":subQ1}),1.0]])]});}
            var Q25;
            {var subQ0=sQuery(id+"F21.wireOp",EDGE,"E122.30.0");var subQ1=sQuery(id+"F21.wireOp",EDGE,"E114");var subQ2=makeQuery(id+"F21.imprint","INTERSECT",VERTEX,{"derivedFrom":[subQ1,subQ0]});Q25=makeQuery(id+"F21.imprint","IMPRINT",FACE,{"disambiguationData":[TD([[makeQuery(id+"F21.imprint","IMPRINT",EDGE,{"disambiguationData":[TD([[subQ2,-1.0]])],"derivedFrom":subQ1}),1.0]])]});}
            var Q26;
            {var subQ0=sQuery(id+"F21.wireOp",EDGE,"E122.29.0");var subQ1=sQuery(id+"F21.wireOp",EDGE,"E115");var subQ2=makeQuery(id+"F21.imprint","INTERSECT",VERTEX,{"derivedFrom":[subQ1,subQ0]});Q26=makeQuery(id+"F21.imprint","IMPRINT",FACE,{"disambiguationData":[TD([[makeQuery(id+"F21.imprint","IMPRINT",EDGE,{"disambiguationData":[TD([[subQ2,-1.0]])],"derivedFrom":subQ1}),1.0]])]});}
            var Q27;
            Q27=makeQuery(id+"F23.opExtrude","CAP_FACE",FACE,{"disambiguationData":[OSD([sQuery(id+"F3.wireOp",EDGE,"E14.0"),sQuery(id+"F3.wireOp",EDGE,"E17"),sQuery(id+"F3.wireOp",EDGE,"E23"),sQuery(id+"F3.wireOp",EDGE,"E24.MirrorCS"),sQuery(id+"F3.wireOp",EDGE,"E25.MirrorCS"),sQuery(id+"F3.wireOp",EDGE,"E26.MirrorCS"),sQuery(id+"F3.wireOp",EDGE,"E28"),sQuery(id+"F3.wireOp",EDGE,"E29"),sQuery(id+"F3.wireOp",EDGE,"E30")])],"isStart":false});
            extrude(context, id + "F41", {"entities" : qUnion([Q0, Q1, Q2, Q3, Q4, Q5, Q6, Q7, Q8, Q9, Q10, Q11, Q12, Q13, Q14, Q15, Q16, Q17, Q18, Q19, Q20, Q21, Q22, Q23, Q24, Q25, Q26, Q27]), "operationType" : NewBodyOperationType.ADD, "depth" : (getVariable(context, 'WT')) * mm});
        }
        {
            var Q0;
            {var subQ0=sQuery(id+"F21.wireOp",EDGE,"E122.17.0");var subQ1=sQuery(id+"F21.wireOp",EDGE,"E114");var subQ2=makeQuery(id+"F21.imprint","INTERSECT",VERTEX,{"derivedFrom":[subQ1,subQ0]});Q0=makeQuery(id+"F21.imprint","IMPRINT",FACE,{"disambiguationData":[TD([[makeQuery(id+"F21.imprint","IMPRINT",EDGE,{"disambiguationData":[TD([[subQ2,-1.0]])],"derivedFrom":subQ1}),1.0]])]});}
            var Q1;
            {var subQ0=sQuery(id+"F21.wireOp",EDGE,"E122.18.0");var subQ1=sQuery(id+"F21.wireOp",EDGE,"E114");var subQ2=makeQuery(id+"F21.imprint","INTERSECT",VERTEX,{"derivedFrom":[subQ1,subQ0]});Q1=makeQuery(id+"F21.imprint","IMPRINT",FACE,{"disambiguationData":[TD([[makeQuery(id+"F21.imprint","IMPRINT",EDGE,{"disambiguationData":[TD([[subQ2,-1.0]])],"derivedFrom":subQ1}),1.0]])]});}
            var Q2;
            {var subQ0=sQuery(id+"F21.wireOp",EDGE,"E122.21.0");var subQ1=sQuery(id+"F21.wireOp",EDGE,"E114");var subQ2=makeQuery(id+"F21.imprint","INTERSECT",VERTEX,{"derivedFrom":[subQ1,subQ0]});Q2=makeQuery(id+"F21.imprint","IMPRINT",FACE,{"disambiguationData":[TD([[makeQuery(id+"F21.imprint","IMPRINT",EDGE,{"disambiguationData":[TD([[subQ2,-1.0]])],"derivedFrom":subQ1}),1.0]])]});}
            var Q3;
            {var subQ0=sQuery(id+"F21.wireOp",EDGE,"E122.22.0");var subQ1=sQuery(id+"F21.wireOp",EDGE,"E114");var subQ2=makeQuery(id+"F21.imprint","INTERSECT",VERTEX,{"derivedFrom":[subQ1,subQ0]});Q3=makeQuery(id+"F21.imprint","IMPRINT",FACE,{"disambiguationData":[TD([[makeQuery(id+"F21.imprint","IMPRINT",EDGE,{"disambiguationData":[TD([[subQ2,-1.0]])],"derivedFrom":subQ1}),1.0]])]});}
            var Q4;
            {var subQ0=sQuery(id+"F21.wireOp",EDGE,"E122.25.0");var subQ1=sQuery(id+"F21.wireOp",EDGE,"E114");var subQ2=makeQuery(id+"F21.imprint","INTERSECT",VERTEX,{"derivedFrom":[subQ1,subQ0]});Q4=makeQuery(id+"F21.imprint","IMPRINT",FACE,{"disambiguationData":[TD([[makeQuery(id+"F21.imprint","IMPRINT",EDGE,{"disambiguationData":[TD([[subQ2,-1.0]])],"derivedFrom":subQ1}),1.0]])]});}
            var Q5;
            {var subQ0=sQuery(id+"F21.wireOp",EDGE,"E122.26.0");var subQ1=sQuery(id+"F21.wireOp",EDGE,"E114");var subQ2=makeQuery(id+"F21.imprint","INTERSECT",VERTEX,{"derivedFrom":[subQ1,subQ0]});Q5=makeQuery(id+"F21.imprint","IMPRINT",FACE,{"disambiguationData":[TD([[makeQuery(id+"F21.imprint","IMPRINT",EDGE,{"disambiguationData":[TD([[subQ2,-1.0]])],"derivedFrom":subQ1}),1.0]])]});}
            var Q6;
            {var subQ0=sQuery(id+"F21.wireOp",EDGE,"E122.29.0");var subQ1=sQuery(id+"F21.wireOp",EDGE,"E114");var subQ2=makeQuery(id+"F21.imprint","INTERSECT",VERTEX,{"derivedFrom":[subQ1,subQ0]});Q6=makeQuery(id+"F21.imprint","IMPRINT",FACE,{"disambiguationData":[TD([[makeQuery(id+"F21.imprint","IMPRINT",EDGE,{"disambiguationData":[TD([[subQ2,-1.0]])],"derivedFrom":subQ1}),1.0]])]});}
            var Q7;
            {var subQ0=sQuery(id+"F21.wireOp",EDGE,"E122.30.0");var subQ1=sQuery(id+"F21.wireOp",EDGE,"E114");var subQ2=makeQuery(id+"F21.imprint","INTERSECT",VERTEX,{"derivedFrom":[subQ1,subQ0]});Q7=makeQuery(id+"F21.imprint","IMPRINT",FACE,{"disambiguationData":[TD([[makeQuery(id+"F21.imprint","IMPRINT",EDGE,{"disambiguationData":[TD([[subQ2,-1.0]])],"derivedFrom":subQ1}),1.0]])]});}
            var Q8;
            {var subQ0=sQuery(id+"F21.wireOp",EDGE,"E122.33.0");var subQ1=sQuery(id+"F21.wireOp",EDGE,"E114");var subQ2=makeQuery(id+"F21.imprint","INTERSECT",VERTEX,{"derivedFrom":[subQ1,subQ0]});Q8=makeQuery(id+"F21.imprint","IMPRINT",FACE,{"disambiguationData":[TD([[makeQuery(id+"F21.imprint","IMPRINT",EDGE,{"disambiguationData":[TD([[subQ2,-1.0]])],"derivedFrom":subQ1}),1.0]])]});}
            var Q9;
            {var subQ0=sQuery(id+"F21.wireOp",EDGE,"E122.34.0");var subQ1=sQuery(id+"F21.wireOp",EDGE,"E114");var subQ2=makeQuery(id+"F21.imprint","INTERSECT",VERTEX,{"derivedFrom":[subQ1,subQ0]});Q9=makeQuery(id+"F21.imprint","IMPRINT",FACE,{"disambiguationData":[TD([[makeQuery(id+"F21.imprint","IMPRINT",EDGE,{"disambiguationData":[TD([[subQ2,-1.0]])],"derivedFrom":subQ1}),1.0]])]});}
            var Q10;
            {var subQ0=sQuery(id+"F21.wireOp",EDGE,"E122.1.0");var subQ1=sQuery(id+"F21.wireOp",EDGE,"E114");var subQ2=makeQuery(id+"F21.imprint","INTERSECT",VERTEX,{"derivedFrom":[subQ1,subQ0]});Q10=makeQuery(id+"F21.imprint","IMPRINT",FACE,{"disambiguationData":[TD([[makeQuery(id+"F21.imprint","IMPRINT",EDGE,{"disambiguationData":[TD([[subQ2,-1.0]])],"derivedFrom":subQ1}),1.0]])]});}
            var Q11;
            {var subQ0=sQuery(id+"F21.wireOp",EDGE,"E122.2.0");var subQ1=sQuery(id+"F21.wireOp",EDGE,"E114");var subQ2=makeQuery(id+"F21.imprint","INTERSECT",VERTEX,{"derivedFrom":[subQ1,subQ0]});Q11=makeQuery(id+"F21.imprint","IMPRINT",FACE,{"disambiguationData":[TD([[makeQuery(id+"F21.imprint","IMPRINT",EDGE,{"disambiguationData":[TD([[subQ2,-1.0]])],"derivedFrom":subQ1}),1.0]])]});}
            var Q12;
            {var subQ0=sQuery(id+"F21.wireOp",EDGE,"E122.5.0");var subQ1=sQuery(id+"F21.wireOp",EDGE,"E114");var subQ2=makeQuery(id+"F21.imprint","INTERSECT",VERTEX,{"derivedFrom":[subQ1,subQ0]});Q12=makeQuery(id+"F21.imprint","IMPRINT",FACE,{"disambiguationData":[TD([[makeQuery(id+"F21.imprint","IMPRINT",EDGE,{"disambiguationData":[TD([[subQ2,-1.0]])],"derivedFrom":subQ1}),1.0]])]});}
            var Q13;
            {var subQ0=sQuery(id+"F21.wireOp",EDGE,"E122.6.0");var subQ1=sQuery(id+"F21.wireOp",EDGE,"E114");var subQ2=makeQuery(id+"F21.imprint","INTERSECT",VERTEX,{"derivedFrom":[subQ1,subQ0]});Q13=makeQuery(id+"F21.imprint","IMPRINT",FACE,{"disambiguationData":[TD([[makeQuery(id+"F21.imprint","IMPRINT",EDGE,{"disambiguationData":[TD([[subQ2,-1.0]])],"derivedFrom":subQ1}),1.0]])]});}
            var Q14;
            {var subQ0=sQuery(id+"F21.wireOp",EDGE,"E122.9.0");var subQ1=sQuery(id+"F21.wireOp",EDGE,"E114");var subQ2=makeQuery(id+"F21.imprint","INTERSECT",VERTEX,{"derivedFrom":[subQ1,subQ0]});Q14=makeQuery(id+"F21.imprint","IMPRINT",FACE,{"disambiguationData":[TD([[makeQuery(id+"F21.imprint","IMPRINT",EDGE,{"disambiguationData":[TD([[subQ2,-1.0]])],"derivedFrom":subQ1}),1.0]])]});}
            var Q15;
            {var subQ0=sQuery(id+"F21.wireOp",EDGE,"E122.10.0");var subQ1=sQuery(id+"F21.wireOp",EDGE,"E114");var subQ2=makeQuery(id+"F21.imprint","INTERSECT",VERTEX,{"derivedFrom":[subQ1,subQ0]});Q15=makeQuery(id+"F21.imprint","IMPRINT",FACE,{"disambiguationData":[TD([[makeQuery(id+"F21.imprint","IMPRINT",EDGE,{"disambiguationData":[TD([[subQ2,-1.0]])],"derivedFrom":subQ1}),1.0]])]});}
            var Q16;
            {var subQ0=sQuery(id+"F21.wireOp",EDGE,"E122.13.0");var subQ1=sQuery(id+"F21.wireOp",EDGE,"E114");var subQ2=makeQuery(id+"F21.imprint","INTERSECT",VERTEX,{"derivedFrom":[subQ1,subQ0]});Q16=makeQuery(id+"F21.imprint","IMPRINT",FACE,{"disambiguationData":[TD([[makeQuery(id+"F21.imprint","IMPRINT",EDGE,{"disambiguationData":[TD([[subQ2,-1.0]])],"derivedFrom":subQ1}),1.0]])]});}
            var Q17;
            {var subQ0=sQuery(id+"F21.wireOp",EDGE,"E122.14.0");var subQ1=sQuery(id+"F21.wireOp",EDGE,"E114");var subQ2=makeQuery(id+"F21.imprint","INTERSECT",VERTEX,{"derivedFrom":[subQ1,subQ0]});Q17=makeQuery(id+"F21.imprint","IMPRINT",FACE,{"disambiguationData":[TD([[makeQuery(id+"F21.imprint","IMPRINT",EDGE,{"disambiguationData":[TD([[subQ2,-1.0]])],"derivedFrom":subQ1}),1.0]])]});}
            var Q18;
            Q18=makeQuery(id+"F21.imprint","IMPRINT",FACE,{"disambiguationData":[TD([[makeQuery(id+"F21.imprint","IMPRINT",EDGE,{"derivedFrom":sQuery(id+"F21.wireOp",EDGE,"E113.0")}),1.0]])]});
            extrude(context, id + "F42", {"entities" : qUnion([Q0, Q1, Q2, Q3, Q4, Q5, Q6, Q7, Q8, Q9, Q10, Q11, Q12, Q13, Q14, Q15, Q16, Q17, Q18]), "oppositeDirection" : true, "depth" : (getVariable(context, 'WT')) * mm});
        }
    });
